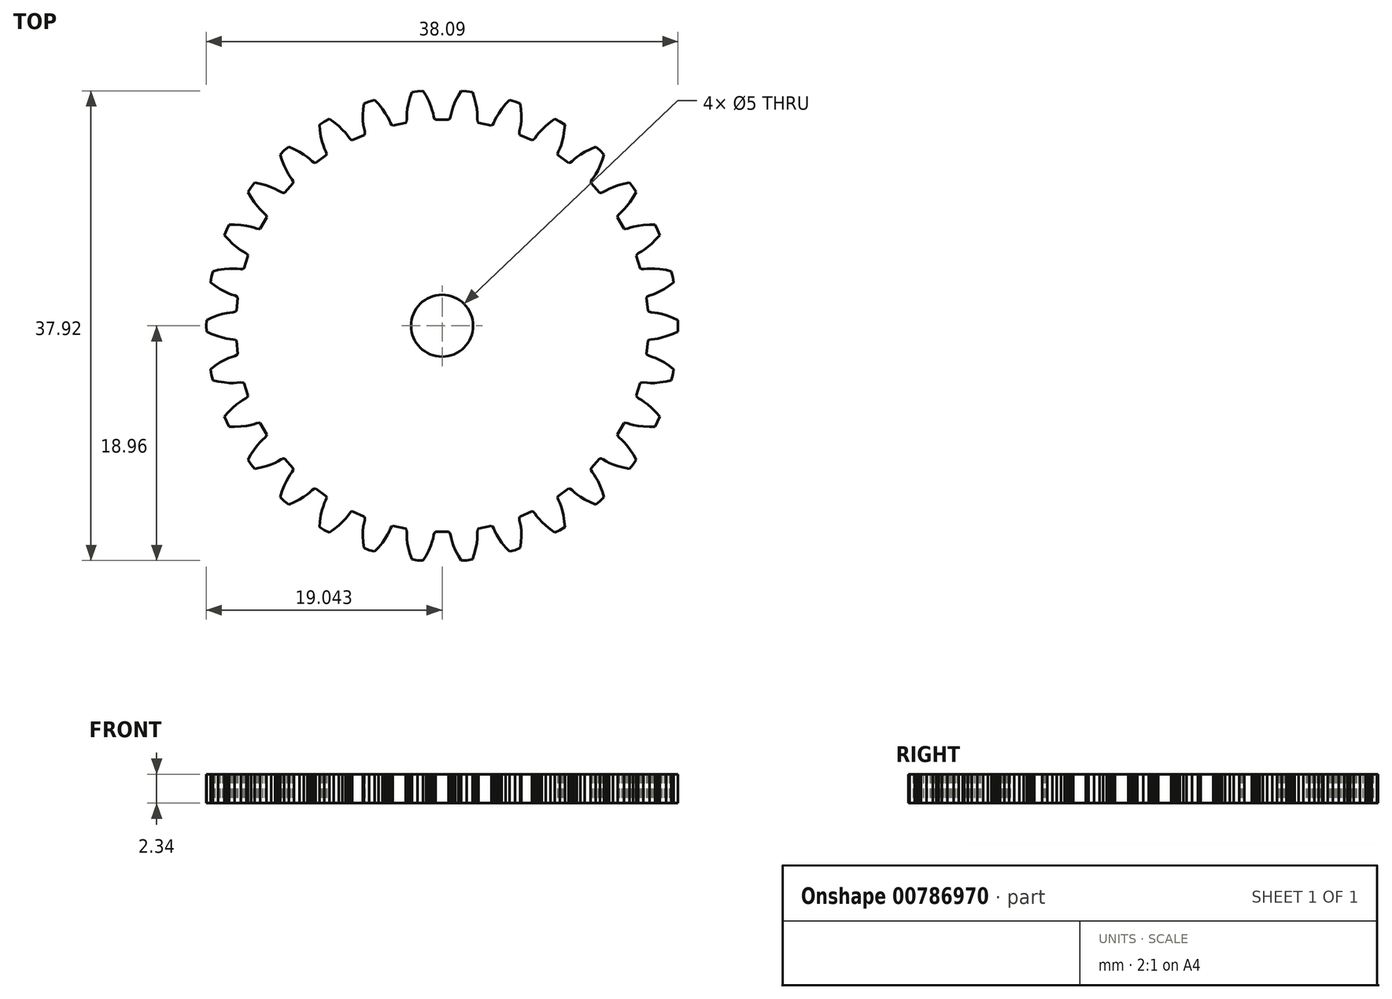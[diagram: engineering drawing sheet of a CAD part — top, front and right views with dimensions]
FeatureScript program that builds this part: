
annotation { "Feature Type Name" : "Feature", "Feature Type Description" : "" }
export const myFeature = defineFeature(function(context is Context, id is Id, definition is map)
    precondition{}
    {
        {
            var Q0;
            Q0=qCreatedBy(makeId("Top.planeOp"),FACE);
            var sketch = newSketch(context, id + "F0", { "sketchPlane" : qUnion([Q0])});
            skLineSegment(sketch, "E0", {"start": v(756.52, -239.33) * mm, "end": v(762.99, -215.17) * mm});
            skLineSegment(sketch, "E1", {"start": v(762.99, -215.17) * mm, "end": v(766.9, -190.46) * mm});
            skLineSegment(sketch, "E2", {"start": v(766.9, -190.46) * mm, "end": v(747.41, -175.84) * mm});
            skLineSegment(sketch, "E3", {"start": v(747.41, -175.84) * mm, "end": v(724.34, -160.92) * mm});
            skLineSegment(sketch, "E4", {"start": v(724.34, -160.92) * mm, "end": v(704.2, -149.81) * mm});
            skLineSegment(sketch, "E5", {"start": v(704.2, -149.81) * mm, "end": v(687.39, -142.02) * mm});
            skLineSegment(sketch, "E6", {"start": v(687.39, -142.02) * mm, "end": v(674.26, -137) * mm});
            skLineSegment(sketch, "E7", {"start": v(674.26, -137) * mm, "end": v(660.16, -132.73) * mm});
            skLineSegment(sketch, "E8", {"start": v(660.16, -132.73) * mm, "end": v(651.05, -128.15) * mm});
            skLineSegment(sketch, "E9", {"start": v(651.05, -128.15) * mm, "end": v(647, -123.28) * mm});
            skLineSegment(sketch, "E10", {"start": v(647, -123.28) * mm, "end": v(653.04, -65.76) * mm});
            skLineSegment(sketch, "E11", {"start": v(653.04, -65.76) * mm, "end": v(658.02, -61.84) * mm});
            skLineSegment(sketch, "E12", {"start": v(658.02, -61.84) * mm, "end": v(667.88, -59.26) * mm});
            skLineSegment(sketch, "E13", {"start": v(667.88, -59.26) * mm, "end": v(682.56, -58) * mm});
            skLineSegment(sketch, "E14", {"start": v(682.56, -58) * mm, "end": v(696.45, -55.83) * mm});
            skLineSegment(sketch, "E15", {"start": v(696.45, -55.83) * mm, "end": v(714.5, -51.7) * mm});
            skLineSegment(sketch, "E16", {"start": v(714.5, -51.7) * mm, "end": v(736.52, -45.02) * mm});
            skLineSegment(sketch, "E17", {"start": v(736.52, -45.02) * mm, "end": v(762.2, -35.23) * mm});
            skLineSegment(sketch, "E18", {"start": v(762.2, -35.23) * mm, "end": v(784.3, -24.98) * mm});
            skLineSegment(sketch, "E19", {"start": v(784.3, -24.98) * mm, "end": v(785.6, 0) * mm});
            skLineSegment(sketch, "E20", {"start": v(785.6, 0) * mm, "end": v(784.3, 24.98) * mm});
            skLineSegment(sketch, "E21", {"start": v(784.3, 24.98) * mm, "end": v(762.2, 35.23) * mm});
            skLineSegment(sketch, "E22", {"start": v(762.2, 35.23) * mm, "end": v(736.52, 45.02) * mm});
            skLineSegment(sketch, "E23", {"start": v(736.52, 45.02) * mm, "end": v(714.5, 51.7) * mm});
            skLineSegment(sketch, "E24", {"start": v(714.5, 51.7) * mm, "end": v(696.45, 55.83) * mm});
            skLineSegment(sketch, "E25", {"start": v(696.45, 55.83) * mm, "end": v(682.56, 58) * mm});
            skLineSegment(sketch, "E26", {"start": v(682.56, 58) * mm, "end": v(667.88, 59.26) * mm});
            skLineSegment(sketch, "E27", {"start": v(667.88, 59.26) * mm, "end": v(658.02, 61.84) * mm});
            skLineSegment(sketch, "E28", {"start": v(658.02, 61.84) * mm, "end": v(653.04, 65.76) * mm});
            skLineSegment(sketch, "E29", {"start": v(653.04, 65.76) * mm, "end": v(647, 123.28) * mm});
            skLineSegment(sketch, "E30", {"start": v(647, 123.28) * mm, "end": v(651.05, 128.15) * mm});
            skLineSegment(sketch, "E31", {"start": v(651.05, 128.15) * mm, "end": v(660.16, 132.73) * mm});
            skLineSegment(sketch, "E32", {"start": v(660.16, 132.73) * mm, "end": v(674.26, 137) * mm});
            skLineSegment(sketch, "E33", {"start": v(674.26, 137) * mm, "end": v(687.39, 142.02) * mm});
            skLineSegment(sketch, "E34", {"start": v(687.39, 142.02) * mm, "end": v(704.2, 149.81) * mm});
            skLineSegment(sketch, "E35", {"start": v(704.2, 149.81) * mm, "end": v(724.34, 160.92) * mm});
            skLineSegment(sketch, "E36", {"start": v(724.34, 160.92) * mm, "end": v(747.41, 175.84) * mm});
            skLineSegment(sketch, "E37", {"start": v(747.41, 175.84) * mm, "end": v(766.9, 190.46) * mm});
            skLineSegment(sketch, "E38", {"start": v(766.9, 190.46) * mm, "end": v(762.99, 215.17) * mm});
            skLineSegment(sketch, "E39", {"start": v(762.99, 215.17) * mm, "end": v(756.52, 239.33) * mm});
            skLineSegment(sketch, "E40", {"start": v(756.52, 239.33) * mm, "end": v(732.77, 244.76) * mm});
            skLineSegment(sketch, "E41", {"start": v(732.77, 244.76) * mm, "end": v(705.62, 249) * mm});
            skLineSegment(sketch, "E42", {"start": v(705.62, 249) * mm, "end": v(682.7, 250.96) * mm});
            skLineSegment(sketch, "E43", {"start": v(682.7, 250.96) * mm, "end": v(664.17, 251.24) * mm});
            skLineSegment(sketch, "E44", {"start": v(664.17, 251.24) * mm, "end": v(650.14, 250.48) * mm});
            skLineSegment(sketch, "E45", {"start": v(650.14, 250.48) * mm, "end": v(635.52, 248.65) * mm});
            skLineSegment(sketch, "E46", {"start": v(635.52, 248.65) * mm, "end": v(625.33, 249.13) * mm});
            skLineSegment(sketch, "E47", {"start": v(625.33, 249.13) * mm, "end": v(619.65, 251.93) * mm});
            skLineSegment(sketch, "E48", {"start": v(619.65, 251.93) * mm, "end": v(601.78, 306.93) * mm});
            skLineSegment(sketch, "E49", {"start": v(601.78, 306.93) * mm, "end": v(604.73, 312.54) * mm});
            skLineSegment(sketch, "E50", {"start": v(604.73, 312.54) * mm, "end": v(612.69, 318.91) * mm});
            skLineSegment(sketch, "E51", {"start": v(612.69, 318.91) * mm, "end": v(625.6, 326.03) * mm});
            skLineSegment(sketch, "E52", {"start": v(625.6, 326.03) * mm, "end": v(637.4, 333.66) * mm});
            skLineSegment(sketch, "E53", {"start": v(637.4, 333.66) * mm, "end": v(652.21, 344.78) * mm});
            skLineSegment(sketch, "E54", {"start": v(652.21, 344.78) * mm, "end": v(669.6, 359.83) * mm});
            skLineSegment(sketch, "E55", {"start": v(669.6, 359.83) * mm, "end": v(689.07, 379.22) * mm});
            skLineSegment(sketch, "E56", {"start": v(689.07, 379.22) * mm, "end": v(705.1, 397.58) * mm});
            skLineSegment(sketch, "E57", {"start": v(705.1, 397.58) * mm, "end": v(696.13, 420.93) * mm});
            skLineSegment(sketch, "E58", {"start": v(696.13, 420.93) * mm, "end": v(684.78, 443.21) * mm});
            skLineSegment(sketch, "E59", {"start": v(684.78, 443.21) * mm, "end": v(660.42, 443.59) * mm});
            skLineSegment(sketch, "E60", {"start": v(660.42, 443.59) * mm, "end": v(632.98, 442.1) * mm});
            skLineSegment(sketch, "E61", {"start": v(632.98, 442.1) * mm, "end": v(610.15, 439.24) * mm});
            skLineSegment(sketch, "E62", {"start": v(610.15, 439.24) * mm, "end": v(591.97, 435.67) * mm});
            skLineSegment(sketch, "E63", {"start": v(591.97, 435.67) * mm, "end": v(578.41, 432) * mm});
            skLineSegment(sketch, "E64", {"start": v(578.41, 432) * mm, "end": v(564.49, 427.18) * mm});
            skLineSegment(sketch, "E65", {"start": v(564.49, 427.18) * mm, "end": v(554.43, 425.53) * mm});
            skLineSegment(sketch, "E66", {"start": v(554.43, 425.53) * mm, "end": v(548.28, 427.08) * mm});
            skLineSegment(sketch, "E67", {"start": v(548.28, 427.08) * mm, "end": v(519.37, 477.17) * mm});
            skLineSegment(sketch, "E68", {"start": v(519.37, 477.17) * mm, "end": v(521.09, 483.27) * mm});
            skLineSegment(sketch, "E69", {"start": v(521.09, 483.27) * mm, "end": v(527.55, 491.16) * mm});
            skLineSegment(sketch, "E70", {"start": v(527.55, 491.16) * mm, "end": v(538.7, 500.8) * mm});
            skLineSegment(sketch, "E71", {"start": v(538.7, 500.8) * mm, "end": v(548.65, 510.72) * mm});
            skLineSegment(sketch, "E72", {"start": v(548.65, 510.72) * mm, "end": v(560.83, 524.67) * mm});
            skLineSegment(sketch, "E73", {"start": v(560.83, 524.67) * mm, "end": v(574.71, 543.02) * mm});
            skLineSegment(sketch, "E74", {"start": v(574.71, 543.02) * mm, "end": v(589.72, 566.03) * mm});
            skLineSegment(sketch, "E75", {"start": v(589.72, 566.03) * mm, "end": v(601.58, 587.32) * mm});
            skLineSegment(sketch, "E76", {"start": v(601.58, 587.32) * mm, "end": v(587.96, 608.3) * mm});
            skLineSegment(sketch, "E77", {"start": v(587.96, 608.3) * mm, "end": v(572.22, 627.73) * mm});
            skLineSegment(sketch, "E78", {"start": v(572.22, 627.73) * mm, "end": v(548.31, 623.03) * mm});
            skLineSegment(sketch, "E79", {"start": v(548.31, 623.03) * mm, "end": v(521.78, 615.87) * mm});
            skLineSegment(sketch, "E80", {"start": v(521.78, 615.87) * mm, "end": v(500.05, 608.33) * mm});
            skLineSegment(sketch, "E81", {"start": v(500.05, 608.33) * mm, "end": v(483.01, 601.06) * mm});
            skLineSegment(sketch, "E82", {"start": v(483.01, 601.06) * mm, "end": v(470.5, 594.65) * mm});
            skLineSegment(sketch, "E83", {"start": v(470.5, 594.65) * mm, "end": v(457.89, 587.04) * mm});
            skLineSegment(sketch, "E84", {"start": v(457.89, 587.04) * mm, "end": v(448.4, 583.33) * mm});
            skLineSegment(sketch, "E85", {"start": v(448.4, 583.33) * mm, "end": v(442.06, 583.58) * mm});
            skLineSegment(sketch, "E86", {"start": v(442.06, 583.58) * mm, "end": v(403.36, 626.56) * mm});
            skLineSegment(sketch, "E87", {"start": v(403.36, 626.56) * mm, "end": v(403.77, 632.88) * mm});
            skLineSegment(sketch, "E88", {"start": v(403.77, 632.88) * mm, "end": v(408.45, 641.94) * mm});
            skLineSegment(sketch, "E89", {"start": v(408.45, 641.94) * mm, "end": v(417.35, 653.69) * mm});
            skLineSegment(sketch, "E90", {"start": v(417.35, 653.69) * mm, "end": v(425.03, 665.46) * mm});
            skLineSegment(sketch, "E91", {"start": v(425.03, 665.46) * mm, "end": v(434.04, 681.64) * mm});
            skLineSegment(sketch, "E92", {"start": v(434.04, 681.64) * mm, "end": v(443.8, 702.47) * mm});
            skLineSegment(sketch, "E93", {"start": v(443.8, 702.47) * mm, "end": v(453.7, 728.1) * mm});
            skLineSegment(sketch, "E94", {"start": v(453.7, 728.1) * mm, "end": v(460.88, 751.39) * mm});
            skLineSegment(sketch, "E95", {"start": v(460.88, 751.39) * mm, "end": v(443.2, 769.07) * mm});
            skLineSegment(sketch, "E96", {"start": v(443.2, 769.07) * mm, "end": v(423.75, 784.81) * mm});
            skLineSegment(sketch, "E97", {"start": v(423.75, 784.81) * mm, "end": v(401.35, 775.25) * mm});
            skLineSegment(sketch, "E98", {"start": v(401.35, 775.25) * mm, "end": v(376.89, 762.72) * mm});
            skLineSegment(sketch, "E99", {"start": v(376.89, 762.72) * mm, "end": v(357.2, 750.83) * mm});
            skLineSegment(sketch, "E100", {"start": v(357.2, 750.83) * mm, "end": v(342.04, 740.18) * mm});
            skLineSegment(sketch, "E101", {"start": v(342.04, 740.18) * mm, "end": v(331.14, 731.31) * mm});
            skLineSegment(sketch, "E102", {"start": v(331.14, 731.31) * mm, "end": v(320.38, 721.24) * mm});
            skLineSegment(sketch, "E103", {"start": v(320.38, 721.24) * mm, "end": v(311.86, 715.64) * mm});
            skLineSegment(sketch, "E104", {"start": v(311.86, 715.64) * mm, "end": v(305.62, 714.56) * mm});
            skLineSegment(sketch, "E105", {"start": v(305.62, 714.56) * mm, "end": v(258.83, 748.56) * mm});
            skLineSegment(sketch, "E106", {"start": v(258.83, 748.56) * mm, "end": v(257.92, 754.83) * mm});
            skLineSegment(sketch, "E107", {"start": v(257.92, 754.83) * mm, "end": v(260.62, 764.66) * mm});
            skLineSegment(sketch, "E108", {"start": v(260.62, 764.66) * mm, "end": v(266.87, 778) * mm});
            skLineSegment(sketch, "E109", {"start": v(266.87, 778) * mm, "end": v(271.93, 791.11) * mm});
            skLineSegment(sketch, "E110", {"start": v(271.93, 791.11) * mm, "end": v(277.39, 808.82) * mm});
            skLineSegment(sketch, "E111", {"start": v(277.39, 808.82) * mm, "end": v(282.6, 831.22) * mm});
            skLineSegment(sketch, "E112", {"start": v(282.6, 831.22) * mm, "end": v(286.96, 858.35) * mm});
            skLineSegment(sketch, "E113", {"start": v(286.96, 858.35) * mm, "end": v(289.14, 882.62) * mm});
            skLineSegment(sketch, "E114", {"start": v(289.14, 882.62) * mm, "end": v(268.16, 896.24) * mm});
            skLineSegment(sketch, "E115", {"start": v(268.16, 896.24) * mm, "end": v(245.87, 907.6) * mm});
            skLineSegment(sketch, "E116", {"start": v(245.87, 907.6) * mm, "end": v(225.94, 893.58) * mm});
            skLineSegment(sketch, "E117", {"start": v(225.94, 893.58) * mm, "end": v(204.63, 876.24) * mm});
            skLineSegment(sketch, "E118", {"start": v(204.63, 876.24) * mm, "end": v(187.83, 860.52) * mm});
            skLineSegment(sketch, "E119", {"start": v(187.83, 860.52) * mm, "end": v(175.23, 846.94) * mm});
            skLineSegment(sketch, "E120", {"start": v(175.23, 846.94) * mm, "end": v(166.4, 836) * mm});
            skLineSegment(sketch, "E121", {"start": v(166.4, 836) * mm, "end": v(157.98, 823.92) * mm});
            skLineSegment(sketch, "E122", {"start": v(157.98, 823.92) * mm, "end": v(150.81, 816.67) * mm});
            skLineSegment(sketch, "E123", {"start": v(150.81, 816.67) * mm, "end": v(144.93, 814.32) * mm});
            skLineSegment(sketch, "E124", {"start": v(144.93, 814.32) * mm, "end": v(92.1, 837.84) * mm});
            skLineSegment(sketch, "E125", {"start": v(92.1, 837.84) * mm, "end": v(89.9, 843.79) * mm});
            skLineSegment(sketch, "E126", {"start": v(89.9, 843.79) * mm, "end": v(90.5, 853.97) * mm});
            skLineSegment(sketch, "E127", {"start": v(90.5, 853.97) * mm, "end": v(93.84, 868.32) * mm});
            skLineSegment(sketch, "E128", {"start": v(93.84, 868.32) * mm, "end": v(96.06, 882.2) * mm});
            skLineSegment(sketch, "E129", {"start": v(96.06, 882.2) * mm, "end": v(97.72, 900.64) * mm});
            skLineSegment(sketch, "E130", {"start": v(97.72, 900.64) * mm, "end": v(98.16, 923.64) * mm});
            skLineSegment(sketch, "E131", {"start": v(98.16, 923.64) * mm, "end": v(96.78, 951.09) * mm});
            skLineSegment(sketch, "E132", {"start": v(96.78, 951.09) * mm, "end": v(93.86, 975.27) * mm});
            skLineSegment(sketch, "E133", {"start": v(93.86, 975.27) * mm, "end": v(70.51, 984.24) * mm});
            skLineSegment(sketch, "E134", {"start": v(70.51, 984.24) * mm, "end": v(46.35, 990.71) * mm});
            skLineSegment(sketch, "E135", {"start": v(46.35, 990.71) * mm, "end": v(29.77, 972.86) * mm});
            skLineSegment(sketch, "E136", {"start": v(29.77, 972.86) * mm, "end": v(12.53, 951.47) * mm});
            skLineSegment(sketch, "E137", {"start": v(12.53, 951.47) * mm, "end": v(-0.63, 932.6) * mm});
            skLineSegment(sketch, "E138", {"start": v(-0.63, 932.6) * mm, "end": v(-10.14, 916.7) * mm});
            skLineSegment(sketch, "E139", {"start": v(-10.14, 916.7) * mm, "end": v(-16.5, 904.17) * mm});
            skLineSegment(sketch, "E140", {"start": v(-16.5, 904.17) * mm, "end": v(-22.22, 890.59) * mm});
            skLineSegment(sketch, "E141", {"start": v(-22.22, 890.59) * mm, "end": v(-27.73, 882) * mm});
            skLineSegment(sketch, "E142", {"start": v(-27.73, 882) * mm, "end": v(-33, 878.49) * mm});
            skLineSegment(sketch, "E143", {"start": v(-33, 878.49) * mm, "end": v(-89.57, 890.51) * mm});
            skLineSegment(sketch, "E144", {"start": v(-89.57, 890.51) * mm, "end": v(-92.95, 895.87) * mm});
            skLineSegment(sketch, "E145", {"start": v(-92.95, 895.87) * mm, "end": v(-94.48, 905.95) * mm});
            skLineSegment(sketch, "E146", {"start": v(-94.48, 905.95) * mm, "end": v(-94.2, 920.68) * mm});
            skLineSegment(sketch, "E147", {"start": v(-94.2, 920.68) * mm, "end": v(-94.9, 934.72) * mm});
            skLineSegment(sketch, "E148", {"start": v(-94.9, 934.72) * mm, "end": v(-97.12, 953.1) * mm});
            skLineSegment(sketch, "E149", {"start": v(-97.12, 953.1) * mm, "end": v(-101.46, 975.7) * mm});
            skLineSegment(sketch, "E150", {"start": v(-101.46, 975.7) * mm, "end": v(-108.52, 1002.25) * mm});
            skLineSegment(sketch, "E151", {"start": v(-108.52, 1002.25) * mm, "end": v(-116.4, 1025.3) * mm});
            skLineSegment(sketch, "E152", {"start": v(-116.4, 1025.3) * mm, "end": v(-141.11, 1029.22) * mm});
            skLineSegment(sketch, "E153", {"start": v(-141.11, 1029.22) * mm, "end": v(-166.09, 1030.53) * mm});
            skLineSegment(sketch, "E154", {"start": v(-166.09, 1030.53) * mm, "end": v(-178.6, 1009.62) * mm});
            skLineSegment(sketch, "E155", {"start": v(-178.6, 1009.62) * mm, "end": v(-191.02, 985.11) * mm});
            skLineSegment(sketch, "E156", {"start": v(-191.02, 985.11) * mm, "end": v(-199.96, 963.92) * mm});
            skLineSegment(sketch, "E157", {"start": v(-199.96, 963.92) * mm, "end": v(-205.96, 946.39) * mm});
            skLineSegment(sketch, "E158", {"start": v(-205.96, 946.39) * mm, "end": v(-209.57, 932.8) * mm});
            skLineSegment(sketch, "E159", {"start": v(-209.57, 932.8) * mm, "end": v(-212.35, 918.34) * mm});
            skLineSegment(sketch, "E160", {"start": v(-212.35, 918.34) * mm, "end": v(-215.95, 908.8) * mm});
            skLineSegment(sketch, "E161", {"start": v(-215.95, 908.8) * mm, "end": v(-220.37, 904.26) * mm});
            skLineSegment(sketch, "E162", {"start": v(-220.37, 904.26) * mm, "end": v(-278.2, 904.26) * mm});
            skLineSegment(sketch, "E163", {"start": v(-278.2, 904.26) * mm, "end": v(-282.62, 908.8) * mm});
            skLineSegment(sketch, "E164", {"start": v(-282.62, 908.8) * mm, "end": v(-286.22, 918.34) * mm});
            skLineSegment(sketch, "E165", {"start": v(-286.22, 918.34) * mm, "end": v(-289, 932.8) * mm});
            skLineSegment(sketch, "E166", {"start": v(-289, 932.8) * mm, "end": v(-292.61, 946.39) * mm});
            skLineSegment(sketch, "E167", {"start": v(-292.61, 946.39) * mm, "end": v(-298.6, 963.92) * mm});
            skLineSegment(sketch, "E168", {"start": v(-298.6, 963.92) * mm, "end": v(-307.55, 985.11) * mm});
            skLineSegment(sketch, "E169", {"start": v(-307.55, 985.11) * mm, "end": v(-319.98, 1009.62) * mm});
            skLineSegment(sketch, "E170", {"start": v(-319.98, 1009.62) * mm, "end": v(-332.48, 1030.53) * mm});
            skLineSegment(sketch, "E171", {"start": v(-332.48, 1030.53) * mm, "end": v(-357.46, 1029.22) * mm});
            skLineSegment(sketch, "E172", {"start": v(-357.46, 1029.22) * mm, "end": v(-382.16, 1025.3) * mm});
            skLineSegment(sketch, "E173", {"start": v(-382.16, 1025.3) * mm, "end": v(-390.05, 1002.25) * mm});
            skLineSegment(sketch, "E174", {"start": v(-390.05, 1002.25) * mm, "end": v(-397.1, 975.7) * mm});
            skLineSegment(sketch, "E175", {"start": v(-397.1, 975.7) * mm, "end": v(-401.45, 953.1) * mm});
            skLineSegment(sketch, "E176", {"start": v(-401.45, 953.1) * mm, "end": v(-403.67, 934.72) * mm});
            skLineSegment(sketch, "E177", {"start": v(-403.67, 934.72) * mm, "end": v(-404.38, 920.68) * mm});
            skLineSegment(sketch, "E178", {"start": v(-404.38, 920.68) * mm, "end": v(-404.09, 905.95) * mm});
            skLineSegment(sketch, "E179", {"start": v(-404.09, 905.95) * mm, "end": v(-405.62, 895.87) * mm});
            skLineSegment(sketch, "E180", {"start": v(-405.62, 895.87) * mm, "end": v(-409, 890.51) * mm});
            skLineSegment(sketch, "E181", {"start": v(-409, 890.51) * mm, "end": v(-465.58, 878.49) * mm});
            skLineSegment(sketch, "E182", {"start": v(-465.58, 878.49) * mm, "end": v(-470.85, 882) * mm});
            skLineSegment(sketch, "E183", {"start": v(-470.85, 882) * mm, "end": v(-476.35, 890.59) * mm});
            skLineSegment(sketch, "E184", {"start": v(-476.35, 890.59) * mm, "end": v(-482.08, 904.17) * mm});
            skLineSegment(sketch, "E185", {"start": v(-482.08, 904.17) * mm, "end": v(-488.43, 916.7) * mm});
            skLineSegment(sketch, "E186", {"start": v(-488.43, 916.7) * mm, "end": v(-497.94, 932.6) * mm});
            skLineSegment(sketch, "E187", {"start": v(-497.94, 932.6) * mm, "end": v(-511.1, 951.47) * mm});
            skLineSegment(sketch, "E188", {"start": v(-511.1, 951.47) * mm, "end": v(-528.35, 972.86) * mm});
            skLineSegment(sketch, "E189", {"start": v(-528.35, 972.86) * mm, "end": v(-544.92, 990.71) * mm});
            skLineSegment(sketch, "E190", {"start": v(-544.92, 990.71) * mm, "end": v(-569.08, 984.24) * mm});
            skLineSegment(sketch, "E191", {"start": v(-569.08, 984.24) * mm, "end": v(-592.43, 975.27) * mm});
            skLineSegment(sketch, "E192", {"start": v(-592.43, 975.27) * mm, "end": v(-595.35, 951.09) * mm});
            skLineSegment(sketch, "E193", {"start": v(-595.35, 951.09) * mm, "end": v(-596.74, 923.64) * mm});
            skLineSegment(sketch, "E194", {"start": v(-596.74, 923.64) * mm, "end": v(-596.29, 900.64) * mm});
            skLineSegment(sketch, "E195", {"start": v(-596.29, 900.64) * mm, "end": v(-594.63, 882.2) * mm});
            skLineSegment(sketch, "E196", {"start": v(-594.63, 882.2) * mm, "end": v(-592.4, 868.32) * mm});
            skLineSegment(sketch, "E197", {"start": v(-592.4, 868.32) * mm, "end": v(-589.06, 853.97) * mm});
            skLineSegment(sketch, "E198", {"start": v(-589.06, 853.97) * mm, "end": v(-588.47, 843.79) * mm});
            skLineSegment(sketch, "E199", {"start": v(-588.47, 843.79) * mm, "end": v(-590.66, 837.84) * mm});
            skLineSegment(sketch, "E200", {"start": v(-590.66, 837.84) * mm, "end": v(-643.5, 814.32) * mm});
            skLineSegment(sketch, "E201", {"start": v(-643.5, 814.32) * mm, "end": v(-649.38, 816.67) * mm});
            skLineSegment(sketch, "E202", {"start": v(-649.38, 816.67) * mm, "end": v(-656.55, 823.92) * mm});
            skLineSegment(sketch, "E203", {"start": v(-656.55, 823.92) * mm, "end": v(-664.98, 836) * mm});
            skLineSegment(sketch, "E204", {"start": v(-664.98, 836) * mm, "end": v(-673.8, 846.94) * mm});
            skLineSegment(sketch, "E205", {"start": v(-673.8, 846.94) * mm, "end": v(-686.4, 860.52) * mm});
            skLineSegment(sketch, "E206", {"start": v(-686.4, 860.52) * mm, "end": v(-703.2, 876.24) * mm});
            skLineSegment(sketch, "E207", {"start": v(-703.2, 876.24) * mm, "end": v(-724.52, 893.58) * mm});
            skLineSegment(sketch, "E208", {"start": v(-724.52, 893.58) * mm, "end": v(-744.44, 907.6) * mm});
            skLineSegment(sketch, "E209", {"start": v(-744.44, 907.6) * mm, "end": v(-766.73, 896.24) * mm});
            skLineSegment(sketch, "E210", {"start": v(-766.73, 896.24) * mm, "end": v(-787.7, 882.62) * mm});
            skLineSegment(sketch, "E211", {"start": v(-787.7, 882.62) * mm, "end": v(-785.53, 858.35) * mm});
            skLineSegment(sketch, "E212", {"start": v(-785.53, 858.35) * mm, "end": v(-781.18, 831.22) * mm});
            skLineSegment(sketch, "E213", {"start": v(-781.18, 831.22) * mm, "end": v(-775.96, 808.82) * mm});
            skLineSegment(sketch, "E214", {"start": v(-775.96, 808.82) * mm, "end": v(-770.5, 791.11) * mm});
            skLineSegment(sketch, "E215", {"start": v(-770.5, 791.11) * mm, "end": v(-765.44, 778) * mm});
            skLineSegment(sketch, "E216", {"start": v(-765.44, 778) * mm, "end": v(-759.19, 764.66) * mm});
            skLineSegment(sketch, "E217", {"start": v(-759.19, 764.66) * mm, "end": v(-756.5, 754.83) * mm});
            skLineSegment(sketch, "E218", {"start": v(-756.5, 754.83) * mm, "end": v(-757.4, 748.56) * mm});
            skLineSegment(sketch, "E219", {"start": v(-757.4, 748.56) * mm, "end": v(-804.2, 714.56) * mm});
            skLineSegment(sketch, "E220", {"start": v(-804.2, 714.56) * mm, "end": v(-810.44, 715.64) * mm});
            skLineSegment(sketch, "E221", {"start": v(-810.44, 715.64) * mm, "end": v(-818.95, 721.24) * mm});
            skLineSegment(sketch, "E222", {"start": v(-818.95, 721.24) * mm, "end": v(-829.71, 731.31) * mm});
            skLineSegment(sketch, "E223", {"start": v(-829.71, 731.31) * mm, "end": v(-840.61, 740.18) * mm});
            skLineSegment(sketch, "E224", {"start": v(-840.61, 740.18) * mm, "end": v(-855.77, 750.83) * mm});
            skLineSegment(sketch, "E225", {"start": v(-855.77, 750.83) * mm, "end": v(-875.46, 762.72) * mm});
            skLineSegment(sketch, "E226", {"start": v(-875.46, 762.72) * mm, "end": v(-899.92, 775.25) * mm});
            skLineSegment(sketch, "E227", {"start": v(-899.92, 775.25) * mm, "end": v(-922.32, 784.81) * mm});
            skLineSegment(sketch, "E228", {"start": v(-922.32, 784.81) * mm, "end": v(-941.76, 769.07) * mm});
            skLineSegment(sketch, "E229", {"start": v(-941.76, 769.07) * mm, "end": v(-959.45, 751.39) * mm});
            skLineSegment(sketch, "E230", {"start": v(-959.45, 751.39) * mm, "end": v(-952.28, 728.1) * mm});
            skLineSegment(sketch, "E231", {"start": v(-952.28, 728.1) * mm, "end": v(-942.38, 702.47) * mm});
            skLineSegment(sketch, "E232", {"start": v(-942.38, 702.47) * mm, "end": v(-932.61, 681.64) * mm});
            skLineSegment(sketch, "E233", {"start": v(-932.61, 681.64) * mm, "end": v(-923.6, 665.46) * mm});
            skLineSegment(sketch, "E234", {"start": v(-923.6, 665.46) * mm, "end": v(-915.92, 653.69) * mm});
            skLineSegment(sketch, "E235", {"start": v(-915.92, 653.69) * mm, "end": v(-907.03, 641.94) * mm});
            skLineSegment(sketch, "E236", {"start": v(-907.03, 641.94) * mm, "end": v(-902.35, 632.88) * mm});
            skLineSegment(sketch, "E237", {"start": v(-902.35, 632.88) * mm, "end": v(-901.93, 626.56) * mm});
            skLineSegment(sketch, "E238", {"start": v(-901.93, 626.56) * mm, "end": v(-940.63, 583.58) * mm});
            skLineSegment(sketch, "E239", {"start": v(-940.63, 583.58) * mm, "end": v(-946.96, 583.33) * mm});
            skLineSegment(sketch, "E240", {"start": v(-946.96, 583.33) * mm, "end": v(-956.46, 587.04) * mm});
            skLineSegment(sketch, "E241", {"start": v(-956.46, 587.04) * mm, "end": v(-969.07, 594.65) * mm});
            skLineSegment(sketch, "E242", {"start": v(-969.07, 594.65) * mm, "end": v(-981.58, 601.06) * mm});
            skLineSegment(sketch, "E243", {"start": v(-981.58, 601.06) * mm, "end": v(-998.62, 608.33) * mm});
            skLineSegment(sketch, "E244", {"start": v(-998.62, 608.33) * mm, "end": v(-1020.35, 615.87) * mm});
            skLineSegment(sketch, "E245", {"start": v(-1020.35, 615.87) * mm, "end": v(-1046.88, 623.03) * mm});
            skLineSegment(sketch, "E246", {"start": v(-1046.88, 623.03) * mm, "end": v(-1070.79, 627.73) * mm});
            skLineSegment(sketch, "E247", {"start": v(-1070.79, 627.73) * mm, "end": v(-1086.53, 608.3) * mm});
            skLineSegment(sketch, "E248", {"start": v(-1086.53, 608.3) * mm, "end": v(-1100.15, 587.32) * mm});
            skLineSegment(sketch, "E249", {"start": v(-1100.15, 587.32) * mm, "end": v(-1088.3, 566.03) * mm});
            skLineSegment(sketch, "E250", {"start": v(-1088.3, 566.03) * mm, "end": v(-1073.28, 543.02) * mm});
            skLineSegment(sketch, "E251", {"start": v(-1073.28, 543.02) * mm, "end": v(-1059.4, 524.67) * mm});
            skLineSegment(sketch, "E252", {"start": v(-1059.4, 524.67) * mm, "end": v(-1047.22, 510.72) * mm});
            skLineSegment(sketch, "E253", {"start": v(-1047.22, 510.72) * mm, "end": v(-1037.26, 500.8) * mm});
            skLineSegment(sketch, "E254", {"start": v(-1037.26, 500.8) * mm, "end": v(-1026.12, 491.16) * mm});
            skLineSegment(sketch, "E255", {"start": v(-1026.12, 491.16) * mm, "end": v(-1019.66, 483.27) * mm});
            skLineSegment(sketch, "E256", {"start": v(-1019.66, 483.27) * mm, "end": v(-1017.94, 477.17) * mm});
            skLineSegment(sketch, "E257", {"start": v(-1017.94, 477.17) * mm, "end": v(-1046.86, 427.08) * mm});
            skLineSegment(sketch, "E258", {"start": v(-1046.86, 427.08) * mm, "end": v(-1053, 425.53) * mm});
            skLineSegment(sketch, "E259", {"start": v(-1053, 425.53) * mm, "end": v(-1063.06, 427.18) * mm});
            skLineSegment(sketch, "E260", {"start": v(-1063.06, 427.18) * mm, "end": v(-1076.98, 432) * mm});
            skLineSegment(sketch, "E261", {"start": v(-1076.98, 432) * mm, "end": v(-1090.55, 435.67) * mm});
            skLineSegment(sketch, "E262", {"start": v(-1090.55, 435.67) * mm, "end": v(-1108.72, 439.24) * mm});
            skLineSegment(sketch, "E263", {"start": v(-1108.72, 439.24) * mm, "end": v(-1131.55, 442.1) * mm});
            skLineSegment(sketch, "E264", {"start": v(-1131.55, 442.1) * mm, "end": v(-1158.99, 443.59) * mm});
            skLineSegment(sketch, "E265", {"start": v(-1158.99, 443.59) * mm, "end": v(-1183.35, 443.21) * mm});
            skLineSegment(sketch, "E266", {"start": v(-1183.35, 443.21) * mm, "end": v(-1194.7, 420.93) * mm});
            skLineSegment(sketch, "E267", {"start": v(-1194.7, 420.93) * mm, "end": v(-1203.67, 397.58) * mm});
            skLineSegment(sketch, "E268", {"start": v(-1203.67, 397.58) * mm, "end": v(-1187.65, 379.22) * mm});
            skLineSegment(sketch, "E269", {"start": v(-1187.65, 379.22) * mm, "end": v(-1168.18, 359.83) * mm});
            skLineSegment(sketch, "E270", {"start": v(-1168.18, 359.83) * mm, "end": v(-1150.78, 344.78) * mm});
            skLineSegment(sketch, "E271", {"start": v(-1150.78, 344.78) * mm, "end": v(-1135.96, 333.66) * mm});
            skLineSegment(sketch, "E272", {"start": v(-1135.96, 333.66) * mm, "end": v(-1124.16, 326.03) * mm});
            skLineSegment(sketch, "E273", {"start": v(-1124.16, 326.03) * mm, "end": v(-1111.26, 318.91) * mm});
            skLineSegment(sketch, "E274", {"start": v(-1111.26, 318.91) * mm, "end": v(-1103.3, 312.54) * mm});
            skLineSegment(sketch, "E275", {"start": v(-1103.3, 312.54) * mm, "end": v(-1100.35, 306.93) * mm});
            skLineSegment(sketch, "E276", {"start": v(-1100.35, 306.93) * mm, "end": v(-1118.22, 251.93) * mm});
            skLineSegment(sketch, "E277", {"start": v(-1118.22, 251.93) * mm, "end": v(-1123.9, 249.13) * mm});
            skLineSegment(sketch, "E278", {"start": v(-1123.9, 249.13) * mm, "end": v(-1134.09, 248.65) * mm});
            skLineSegment(sketch, "E279", {"start": v(-1134.09, 248.65) * mm, "end": v(-1148.71, 250.48) * mm});
            skLineSegment(sketch, "E280", {"start": v(-1148.71, 250.48) * mm, "end": v(-1162.74, 251.24) * mm});
            skLineSegment(sketch, "E281", {"start": v(-1162.74, 251.24) * mm, "end": v(-1181.27, 250.96) * mm});
            skLineSegment(sketch, "E282", {"start": v(-1181.27, 250.96) * mm, "end": v(-1204.19, 249) * mm});
            skLineSegment(sketch, "E283", {"start": v(-1204.19, 249) * mm, "end": v(-1231.34, 244.76) * mm});
            skLineSegment(sketch, "E284", {"start": v(-1231.34, 244.76) * mm, "end": v(-1255.09, 239.33) * mm});
            skLineSegment(sketch, "E285", {"start": v(-1255.09, 239.33) * mm, "end": v(-1261.56, 215.17) * mm});
            skLineSegment(sketch, "E286", {"start": v(-1261.56, 215.17) * mm, "end": v(-1265.47, 190.46) * mm});
            skLineSegment(sketch, "E287", {"start": v(-1265.47, 190.46) * mm, "end": v(-1245.99, 175.84) * mm});
            skLineSegment(sketch, "E288", {"start": v(-1245.99, 175.84) * mm, "end": v(-1222.9, 160.92) * mm});
            skLineSegment(sketch, "E289", {"start": v(-1222.9, 160.92) * mm, "end": v(-1202.77, 149.81) * mm});
            skLineSegment(sketch, "E290", {"start": v(-1202.77, 149.81) * mm, "end": v(-1185.96, 142.02) * mm});
            skLineSegment(sketch, "E291", {"start": v(-1185.96, 142.02) * mm, "end": v(-1172.83, 137) * mm});
            skLineSegment(sketch, "E292", {"start": v(-1172.83, 137) * mm, "end": v(-1158.73, 132.73) * mm});
            skLineSegment(sketch, "E293", {"start": v(-1158.73, 132.73) * mm, "end": v(-1149.62, 128.15) * mm});
            skLineSegment(sketch, "E294", {"start": v(-1149.62, 128.15) * mm, "end": v(-1145.57, 123.28) * mm});
            skLineSegment(sketch, "E295", {"start": v(-1145.57, 123.28) * mm, "end": v(-1151.61, 65.76) * mm});
            skLineSegment(sketch, "E296", {"start": v(-1151.61, 65.76) * mm, "end": v(-1156.59, 61.84) * mm});
            skLineSegment(sketch, "E297", {"start": v(-1156.59, 61.84) * mm, "end": v(-1166.45, 59.26) * mm});
            skLineSegment(sketch, "E298", {"start": v(-1166.45, 59.26) * mm, "end": v(-1181.14, 58) * mm});
            skLineSegment(sketch, "E299", {"start": v(-1181.14, 58) * mm, "end": v(-1195.02, 55.83) * mm});
            skLineSegment(sketch, "E300", {"start": v(-1195.02, 55.83) * mm, "end": v(-1213.08, 51.7) * mm});
            skLineSegment(sketch, "E301", {"start": v(-1213.08, 51.7) * mm, "end": v(-1235.09, 45.02) * mm});
            skLineSegment(sketch, "E302", {"start": v(-1235.09, 45.02) * mm, "end": v(-1260.76, 35.23) * mm});
            skLineSegment(sketch, "E303", {"start": v(-1260.76, 35.23) * mm, "end": v(-1282.87, 24.98) * mm});
            skLineSegment(sketch, "E304", {"start": v(-1282.87, 24.98) * mm, "end": v(-1284.17, 0) * mm});
            skLineSegment(sketch, "E305", {"start": v(-1284.17, 0) * mm, "end": v(-1282.87, -24.98) * mm});
            skLineSegment(sketch, "E306", {"start": v(-1282.87, -24.98) * mm, "end": v(-1260.76, -35.23) * mm});
            skLineSegment(sketch, "E307", {"start": v(-1260.76, -35.23) * mm, "end": v(-1235.09, -45.02) * mm});
            skLineSegment(sketch, "E308", {"start": v(-1235.09, -45.02) * mm, "end": v(-1213.08, -51.7) * mm});
            skLineSegment(sketch, "E309", {"start": v(-1213.08, -51.7) * mm, "end": v(-1195.02, -55.83) * mm});
            skLineSegment(sketch, "E310", {"start": v(-1195.02, -55.83) * mm, "end": v(-1181.14, -58) * mm});
            skLineSegment(sketch, "E311", {"start": v(-1181.14, -58) * mm, "end": v(-1166.45, -59.26) * mm});
            skLineSegment(sketch, "E312", {"start": v(-1166.45, -59.26) * mm, "end": v(-1156.59, -61.84) * mm});
            skLineSegment(sketch, "E313", {"start": v(-1156.59, -61.84) * mm, "end": v(-1151.61, -65.76) * mm});
            skLineSegment(sketch, "E314", {"start": v(-1151.61, -65.76) * mm, "end": v(-1145.57, -123.28) * mm});
            skLineSegment(sketch, "E315", {"start": v(-1145.57, -123.28) * mm, "end": v(-1149.62, -128.15) * mm});
            skLineSegment(sketch, "E316", {"start": v(-1149.62, -128.15) * mm, "end": v(-1158.73, -132.73) * mm});
            skLineSegment(sketch, "E317", {"start": v(-1158.73, -132.73) * mm, "end": v(-1172.83, -137) * mm});
            skLineSegment(sketch, "E318", {"start": v(-1172.83, -137) * mm, "end": v(-1185.96, -142.02) * mm});
            skLineSegment(sketch, "E319", {"start": v(-1185.96, -142.02) * mm, "end": v(-1202.77, -149.81) * mm});
            skLineSegment(sketch, "E320", {"start": v(-1202.77, -149.81) * mm, "end": v(-1222.9, -160.92) * mm});
            skLineSegment(sketch, "E321", {"start": v(-1222.9, -160.92) * mm, "end": v(-1245.99, -175.84) * mm});
            skLineSegment(sketch, "E322", {"start": v(-1245.99, -175.84) * mm, "end": v(-1265.47, -190.46) * mm});
            skLineSegment(sketch, "E323", {"start": v(-1265.47, -190.46) * mm, "end": v(-1261.56, -215.17) * mm});
            skLineSegment(sketch, "E324", {"start": v(-1261.56, -215.17) * mm, "end": v(-1255.09, -239.33) * mm});
            skLineSegment(sketch, "E325", {"start": v(-1255.09, -239.33) * mm, "end": v(-1231.34, -244.76) * mm});
            skLineSegment(sketch, "E326", {"start": v(-1231.34, -244.76) * mm, "end": v(-1204.19, -249) * mm});
            skLineSegment(sketch, "E327", {"start": v(-1204.19, -249) * mm, "end": v(-1181.27, -250.96) * mm});
            skLineSegment(sketch, "E328", {"start": v(-1181.27, -250.96) * mm, "end": v(-1162.74, -251.24) * mm});
            skLineSegment(sketch, "E329", {"start": v(-1162.74, -251.24) * mm, "end": v(-1148.71, -250.48) * mm});
            skLineSegment(sketch, "E330", {"start": v(-1148.71, -250.48) * mm, "end": v(-1134.09, -248.65) * mm});
            skLineSegment(sketch, "E331", {"start": v(-1134.09, -248.65) * mm, "end": v(-1123.9, -249.13) * mm});
            skLineSegment(sketch, "E332", {"start": v(-1123.9, -249.13) * mm, "end": v(-1118.22, -251.93) * mm});
            skLineSegment(sketch, "E333", {"start": v(-1118.22, -251.93) * mm, "end": v(-1100.35, -306.93) * mm});
            skLineSegment(sketch, "E334", {"start": v(-1100.35, -306.93) * mm, "end": v(-1103.3, -312.54) * mm});
            skLineSegment(sketch, "E335", {"start": v(-1103.3, -312.54) * mm, "end": v(-1111.26, -318.91) * mm});
            skLineSegment(sketch, "E336", {"start": v(-1111.26, -318.91) * mm, "end": v(-1124.16, -326.03) * mm});
            skLineSegment(sketch, "E337", {"start": v(-1124.16, -326.03) * mm, "end": v(-1135.96, -333.66) * mm});
            skLineSegment(sketch, "E338", {"start": v(-1135.96, -333.66) * mm, "end": v(-1150.78, -344.78) * mm});
            skLineSegment(sketch, "E339", {"start": v(-1150.78, -344.78) * mm, "end": v(-1168.18, -359.83) * mm});
            skLineSegment(sketch, "E340", {"start": v(-1168.18, -359.83) * mm, "end": v(-1187.65, -379.22) * mm});
            skLineSegment(sketch, "E341", {"start": v(-1187.65, -379.22) * mm, "end": v(-1203.67, -397.58) * mm});
            skLineSegment(sketch, "E342", {"start": v(-1203.67, -397.58) * mm, "end": v(-1194.7, -420.93) * mm});
            skLineSegment(sketch, "E343", {"start": v(-1194.7, -420.93) * mm, "end": v(-1183.35, -443.21) * mm});
            skLineSegment(sketch, "E344", {"start": v(-1183.35, -443.21) * mm, "end": v(-1158.99, -443.59) * mm});
            skLineSegment(sketch, "E345", {"start": v(-1158.99, -443.59) * mm, "end": v(-1131.55, -442.1) * mm});
            skLineSegment(sketch, "E346", {"start": v(-1131.55, -442.1) * mm, "end": v(-1108.72, -439.24) * mm});
            skLineSegment(sketch, "E347", {"start": v(-1108.72, -439.24) * mm, "end": v(-1090.55, -435.67) * mm});
            skLineSegment(sketch, "E348", {"start": v(-1090.55, -435.67) * mm, "end": v(-1076.98, -432) * mm});
            skLineSegment(sketch, "E349", {"start": v(-1076.98, -432) * mm, "end": v(-1063.06, -427.18) * mm});
            skLineSegment(sketch, "E350", {"start": v(-1063.06, -427.18) * mm, "end": v(-1053, -425.53) * mm});
            skLineSegment(sketch, "E351", {"start": v(-1053, -425.53) * mm, "end": v(-1046.86, -427.08) * mm});
            skLineSegment(sketch, "E352", {"start": v(-1046.86, -427.08) * mm, "end": v(-1017.94, -477.17) * mm});
            skLineSegment(sketch, "E353", {"start": v(-1017.94, -477.17) * mm, "end": v(-1019.66, -483.27) * mm});
            skLineSegment(sketch, "E354", {"start": v(-1019.66, -483.27) * mm, "end": v(-1026.12, -491.16) * mm});
            skLineSegment(sketch, "E355", {"start": v(-1026.12, -491.16) * mm, "end": v(-1037.26, -500.8) * mm});
            skLineSegment(sketch, "E356", {"start": v(-1037.26, -500.8) * mm, "end": v(-1047.22, -510.72) * mm});
            skLineSegment(sketch, "E357", {"start": v(-1047.22, -510.72) * mm, "end": v(-1059.4, -524.67) * mm});
            skLineSegment(sketch, "E358", {"start": v(-1059.4, -524.67) * mm, "end": v(-1073.28, -543.02) * mm});
            skLineSegment(sketch, "E359", {"start": v(-1073.28, -543.02) * mm, "end": v(-1088.3, -566.03) * mm});
            skLineSegment(sketch, "E360", {"start": v(-1088.3, -566.03) * mm, "end": v(-1100.15, -587.32) * mm});
            skLineSegment(sketch, "E361", {"start": v(-1100.15, -587.32) * mm, "end": v(-1086.53, -608.3) * mm});
            skLineSegment(sketch, "E362", {"start": v(-1086.53, -608.3) * mm, "end": v(-1070.79, -627.73) * mm});
            skLineSegment(sketch, "E363", {"start": v(-1070.79, -627.73) * mm, "end": v(-1046.88, -623.03) * mm});
            skLineSegment(sketch, "E364", {"start": v(-1046.88, -623.03) * mm, "end": v(-1020.35, -615.87) * mm});
            skLineSegment(sketch, "E365", {"start": v(-1020.35, -615.87) * mm, "end": v(-998.62, -608.33) * mm});
            skLineSegment(sketch, "E366", {"start": v(-998.62, -608.33) * mm, "end": v(-981.58, -601.06) * mm});
            skLineSegment(sketch, "E367", {"start": v(-981.58, -601.06) * mm, "end": v(-969.07, -594.65) * mm});
            skLineSegment(sketch, "E368", {"start": v(-969.07, -594.65) * mm, "end": v(-956.46, -587.04) * mm});
            skLineSegment(sketch, "E369", {"start": v(-956.46, -587.04) * mm, "end": v(-946.96, -583.33) * mm});
            skLineSegment(sketch, "E370", {"start": v(-946.96, -583.33) * mm, "end": v(-940.63, -583.58) * mm});
            skLineSegment(sketch, "E371", {"start": v(-940.63, -583.58) * mm, "end": v(-901.93, -626.56) * mm});
            skLineSegment(sketch, "E372", {"start": v(-901.93, -626.56) * mm, "end": v(-902.35, -632.88) * mm});
            skLineSegment(sketch, "E373", {"start": v(-902.35, -632.88) * mm, "end": v(-907.03, -641.94) * mm});
            skLineSegment(sketch, "E374", {"start": v(-907.03, -641.94) * mm, "end": v(-915.92, -653.69) * mm});
            skLineSegment(sketch, "E375", {"start": v(-915.92, -653.69) * mm, "end": v(-923.6, -665.46) * mm});
            skLineSegment(sketch, "E376", {"start": v(-923.6, -665.46) * mm, "end": v(-932.61, -681.64) * mm});
            skLineSegment(sketch, "E377", {"start": v(-932.61, -681.64) * mm, "end": v(-942.38, -702.47) * mm});
            skLineSegment(sketch, "E378", {"start": v(-942.38, -702.47) * mm, "end": v(-952.28, -728.1) * mm});
            skLineSegment(sketch, "E379", {"start": v(-952.28, -728.1) * mm, "end": v(-959.45, -751.39) * mm});
            skLineSegment(sketch, "E380", {"start": v(-959.45, -751.39) * mm, "end": v(-941.76, -769.07) * mm});
            skLineSegment(sketch, "E381", {"start": v(-941.76, -769.07) * mm, "end": v(-922.32, -784.81) * mm});
            skLineSegment(sketch, "E382", {"start": v(-922.32, -784.81) * mm, "end": v(-899.92, -775.25) * mm});
            skLineSegment(sketch, "E383", {"start": v(-899.92, -775.25) * mm, "end": v(-875.46, -762.72) * mm});
            skLineSegment(sketch, "E384", {"start": v(-875.46, -762.72) * mm, "end": v(-855.77, -750.83) * mm});
            skLineSegment(sketch, "E385", {"start": v(-855.77, -750.83) * mm, "end": v(-840.61, -740.18) * mm});
            skLineSegment(sketch, "E386", {"start": v(-840.61, -740.18) * mm, "end": v(-829.71, -731.31) * mm});
            skLineSegment(sketch, "E387", {"start": v(-829.71, -731.31) * mm, "end": v(-818.95, -721.24) * mm});
            skLineSegment(sketch, "E388", {"start": v(-818.95, -721.24) * mm, "end": v(-810.44, -715.64) * mm});
            skLineSegment(sketch, "E389", {"start": v(-810.44, -715.64) * mm, "end": v(-804.2, -714.56) * mm});
            skLineSegment(sketch, "E390", {"start": v(-804.2, -714.56) * mm, "end": v(-757.4, -748.56) * mm});
            skLineSegment(sketch, "E391", {"start": v(-757.4, -748.56) * mm, "end": v(-756.5, -754.83) * mm});
            skLineSegment(sketch, "E392", {"start": v(-756.5, -754.83) * mm, "end": v(-759.19, -764.66) * mm});
            skLineSegment(sketch, "E393", {"start": v(-759.19, -764.66) * mm, "end": v(-765.44, -778) * mm});
            skLineSegment(sketch, "E394", {"start": v(-765.44, -778) * mm, "end": v(-770.5, -791.11) * mm});
            skLineSegment(sketch, "E395", {"start": v(-770.5, -791.11) * mm, "end": v(-775.96, -808.82) * mm});
            skLineSegment(sketch, "E396", {"start": v(-775.96, -808.82) * mm, "end": v(-781.18, -831.22) * mm});
            skLineSegment(sketch, "E397", {"start": v(-781.18, -831.22) * mm, "end": v(-785.53, -858.35) * mm});
            skLineSegment(sketch, "E398", {"start": v(-785.53, -858.35) * mm, "end": v(-787.7, -882.62) * mm});
            skLineSegment(sketch, "E399", {"start": v(-787.7, -882.62) * mm, "end": v(-766.73, -896.24) * mm});
            skLineSegment(sketch, "E400", {"start": v(-766.73, -896.24) * mm, "end": v(-744.44, -907.6) * mm});
            skLineSegment(sketch, "E401", {"start": v(-744.44, -907.6) * mm, "end": v(-724.52, -893.58) * mm});
            skLineSegment(sketch, "E402", {"start": v(-724.52, -893.58) * mm, "end": v(-703.2, -876.24) * mm});
            skLineSegment(sketch, "E403", {"start": v(-703.2, -876.24) * mm, "end": v(-686.4, -860.52) * mm});
            skLineSegment(sketch, "E404", {"start": v(-686.4, -860.52) * mm, "end": v(-673.8, -846.94) * mm});
            skLineSegment(sketch, "E405", {"start": v(-673.8, -846.94) * mm, "end": v(-664.98, -836) * mm});
            skLineSegment(sketch, "E406", {"start": v(-664.98, -836) * mm, "end": v(-656.55, -823.92) * mm});
            skLineSegment(sketch, "E407", {"start": v(-656.55, -823.92) * mm, "end": v(-649.38, -816.67) * mm});
            skLineSegment(sketch, "E408", {"start": v(-649.38, -816.67) * mm, "end": v(-643.5, -814.32) * mm});
            skLineSegment(sketch, "E409", {"start": v(-643.5, -814.32) * mm, "end": v(-590.66, -837.84) * mm});
            skLineSegment(sketch, "E410", {"start": v(-590.66, -837.84) * mm, "end": v(-588.47, -843.79) * mm});
            skLineSegment(sketch, "E411", {"start": v(-588.47, -843.79) * mm, "end": v(-589.06, -853.97) * mm});
            skLineSegment(sketch, "E412", {"start": v(-589.06, -853.97) * mm, "end": v(-592.4, -868.32) * mm});
            skLineSegment(sketch, "E413", {"start": v(-592.4, -868.32) * mm, "end": v(-594.63, -882.2) * mm});
            skLineSegment(sketch, "E414", {"start": v(-594.63, -882.2) * mm, "end": v(-596.29, -900.64) * mm});
            skLineSegment(sketch, "E415", {"start": v(-596.29, -900.64) * mm, "end": v(-596.74, -923.64) * mm});
            skLineSegment(sketch, "E416", {"start": v(-596.74, -923.64) * mm, "end": v(-595.35, -951.09) * mm});
            skLineSegment(sketch, "E417", {"start": v(-595.35, -951.09) * mm, "end": v(-592.43, -975.27) * mm});
            skLineSegment(sketch, "E418", {"start": v(-592.43, -975.27) * mm, "end": v(-569.08, -984.24) * mm});
            skLineSegment(sketch, "E419", {"start": v(-569.08, -984.24) * mm, "end": v(-544.92, -990.71) * mm});
            skLineSegment(sketch, "E420", {"start": v(-544.92, -990.71) * mm, "end": v(-528.35, -972.86) * mm});
            skLineSegment(sketch, "E421", {"start": v(-528.35, -972.86) * mm, "end": v(-511.1, -951.47) * mm});
            skLineSegment(sketch, "E422", {"start": v(-511.1, -951.47) * mm, "end": v(-497.94, -932.6) * mm});
            skLineSegment(sketch, "E423", {"start": v(-497.94, -932.6) * mm, "end": v(-488.43, -916.7) * mm});
            skLineSegment(sketch, "E424", {"start": v(-488.43, -916.7) * mm, "end": v(-482.08, -904.17) * mm});
            skLineSegment(sketch, "E425", {"start": v(-482.08, -904.17) * mm, "end": v(-476.35, -890.59) * mm});
            skLineSegment(sketch, "E426", {"start": v(-476.35, -890.59) * mm, "end": v(-470.85, -882) * mm});
            skLineSegment(sketch, "E427", {"start": v(-470.85, -882) * mm, "end": v(-465.58, -878.49) * mm});
            skLineSegment(sketch, "E428", {"start": v(-465.58, -878.49) * mm, "end": v(-409, -890.51) * mm});
            skLineSegment(sketch, "E429", {"start": v(-409, -890.51) * mm, "end": v(-405.62, -895.87) * mm});
            skLineSegment(sketch, "E430", {"start": v(-405.62, -895.87) * mm, "end": v(-404.09, -905.95) * mm});
            skLineSegment(sketch, "E431", {"start": v(-404.09, -905.95) * mm, "end": v(-404.38, -920.68) * mm});
            skLineSegment(sketch, "E432", {"start": v(-404.38, -920.68) * mm, "end": v(-403.67, -934.72) * mm});
            skLineSegment(sketch, "E433", {"start": v(-403.67, -934.72) * mm, "end": v(-401.45, -953.1) * mm});
            skLineSegment(sketch, "E434", {"start": v(-401.45, -953.1) * mm, "end": v(-397.1, -975.7) * mm});
            skLineSegment(sketch, "E435", {"start": v(-397.1, -975.7) * mm, "end": v(-390.05, -1002.25) * mm});
            skLineSegment(sketch, "E436", {"start": v(-390.05, -1002.25) * mm, "end": v(-382.16, -1025.3) * mm});
            skLineSegment(sketch, "E437", {"start": v(-382.16, -1025.3) * mm, "end": v(-357.46, -1029.22) * mm});
            skLineSegment(sketch, "E438", {"start": v(-357.46, -1029.22) * mm, "end": v(-332.48, -1030.53) * mm});
            skLineSegment(sketch, "E439", {"start": v(-332.48, -1030.53) * mm, "end": v(-319.98, -1009.62) * mm});
            skLineSegment(sketch, "E440", {"start": v(-319.98, -1009.62) * mm, "end": v(-307.55, -985.11) * mm});
            skLineSegment(sketch, "E441", {"start": v(-307.55, -985.11) * mm, "end": v(-298.6, -963.92) * mm});
            skLineSegment(sketch, "E442", {"start": v(-298.6, -963.92) * mm, "end": v(-292.61, -946.39) * mm});
            skLineSegment(sketch, "E443", {"start": v(-292.61, -946.39) * mm, "end": v(-289, -932.8) * mm});
            skLineSegment(sketch, "E444", {"start": v(-289, -932.8) * mm, "end": v(-286.22, -918.34) * mm});
            skLineSegment(sketch, "E445", {"start": v(-286.22, -918.34) * mm, "end": v(-282.62, -908.8) * mm});
            skLineSegment(sketch, "E446", {"start": v(-282.62, -908.8) * mm, "end": v(-278.2, -904.26) * mm});
            skLineSegment(sketch, "E447", {"start": v(-278.2, -904.26) * mm, "end": v(-220.37, -904.26) * mm});
            skLineSegment(sketch, "E448", {"start": v(-220.37, -904.26) * mm, "end": v(-215.95, -908.8) * mm});
            skLineSegment(sketch, "E449", {"start": v(-215.95, -908.8) * mm, "end": v(-212.35, -918.34) * mm});
            skLineSegment(sketch, "E450", {"start": v(-212.35, -918.34) * mm, "end": v(-209.57, -932.8) * mm});
            skLineSegment(sketch, "E451", {"start": v(-209.57, -932.8) * mm, "end": v(-205.96, -946.39) * mm});
            skLineSegment(sketch, "E452", {"start": v(-205.96, -946.39) * mm, "end": v(-199.96, -963.92) * mm});
            skLineSegment(sketch, "E453", {"start": v(-199.96, -963.92) * mm, "end": v(-191.02, -985.11) * mm});
            skLineSegment(sketch, "E454", {"start": v(-191.02, -985.11) * mm, "end": v(-178.6, -1009.62) * mm});
            skLineSegment(sketch, "E455", {"start": v(-178.6, -1009.62) * mm, "end": v(-166.09, -1030.53) * mm});
            skLineSegment(sketch, "E456", {"start": v(-166.09, -1030.53) * mm, "end": v(-141.11, -1029.22) * mm});
            skLineSegment(sketch, "E457", {"start": v(-141.11, -1029.22) * mm, "end": v(-116.4, -1025.3) * mm});
            skLineSegment(sketch, "E458", {"start": v(-116.4, -1025.3) * mm, "end": v(-108.52, -1002.25) * mm});
            skLineSegment(sketch, "E459", {"start": v(-108.52, -1002.25) * mm, "end": v(-101.46, -975.7) * mm});
            skLineSegment(sketch, "E460", {"start": v(-101.46, -975.7) * mm, "end": v(-97.12, -953.1) * mm});
            skLineSegment(sketch, "E461", {"start": v(-97.12, -953.1) * mm, "end": v(-94.9, -934.72) * mm});
            skLineSegment(sketch, "E462", {"start": v(-94.9, -934.72) * mm, "end": v(-94.2, -920.68) * mm});
            skLineSegment(sketch, "E463", {"start": v(-94.2, -920.68) * mm, "end": v(-94.48, -905.95) * mm});
            skLineSegment(sketch, "E464", {"start": v(-94.48, -905.95) * mm, "end": v(-92.95, -895.87) * mm});
            skLineSegment(sketch, "E465", {"start": v(-92.95, -895.87) * mm, "end": v(-89.57, -890.51) * mm});
            skLineSegment(sketch, "E466", {"start": v(-89.57, -890.51) * mm, "end": v(-33, -878.49) * mm});
            skLineSegment(sketch, "E467", {"start": v(-33, -878.49) * mm, "end": v(-27.73, -882) * mm});
            skLineSegment(sketch, "E468", {"start": v(-27.73, -882) * mm, "end": v(-22.22, -890.59) * mm});
            skLineSegment(sketch, "E469", {"start": v(-22.22, -890.59) * mm, "end": v(-16.5, -904.17) * mm});
            skLineSegment(sketch, "E470", {"start": v(-16.5, -904.17) * mm, "end": v(-10.14, -916.7) * mm});
            skLineSegment(sketch, "E471", {"start": v(-10.14, -916.7) * mm, "end": v(-0.63, -932.6) * mm});
            skLineSegment(sketch, "E472", {"start": v(-0.63, -932.6) * mm, "end": v(12.53, -951.47) * mm});
            skLineSegment(sketch, "E473", {"start": v(12.53, -951.47) * mm, "end": v(29.77, -972.86) * mm});
            skLineSegment(sketch, "E474", {"start": v(29.77, -972.86) * mm, "end": v(46.35, -990.71) * mm});
            skLineSegment(sketch, "E475", {"start": v(46.35, -990.71) * mm, "end": v(70.51, -984.24) * mm});
            skLineSegment(sketch, "E476", {"start": v(70.51, -984.24) * mm, "end": v(93.86, -975.27) * mm});
            skLineSegment(sketch, "E477", {"start": v(93.86, -975.27) * mm, "end": v(96.78, -951.09) * mm});
            skLineSegment(sketch, "E478", {"start": v(96.78, -951.09) * mm, "end": v(98.16, -923.64) * mm});
            skLineSegment(sketch, "E479", {"start": v(98.16, -923.64) * mm, "end": v(97.72, -900.64) * mm});
            skLineSegment(sketch, "E480", {"start": v(97.72, -900.64) * mm, "end": v(96.06, -882.2) * mm});
            skLineSegment(sketch, "E481", {"start": v(96.06, -882.2) * mm, "end": v(93.84, -868.32) * mm});
            skLineSegment(sketch, "E482", {"start": v(93.84, -868.32) * mm, "end": v(90.5, -853.97) * mm});
            skLineSegment(sketch, "E483", {"start": v(90.5, -853.97) * mm, "end": v(89.9, -843.79) * mm});
            skLineSegment(sketch, "E484", {"start": v(89.9, -843.79) * mm, "end": v(92.1, -837.84) * mm});
            skLineSegment(sketch, "E485", {"start": v(92.1, -837.84) * mm, "end": v(144.93, -814.32) * mm});
            skLineSegment(sketch, "E486", {"start": v(144.93, -814.32) * mm, "end": v(150.81, -816.67) * mm});
            skLineSegment(sketch, "E487", {"start": v(150.81, -816.67) * mm, "end": v(157.98, -823.92) * mm});
            skLineSegment(sketch, "E488", {"start": v(157.98, -823.92) * mm, "end": v(166.4, -836) * mm});
            skLineSegment(sketch, "E489", {"start": v(166.4, -836) * mm, "end": v(175.23, -846.94) * mm});
            skLineSegment(sketch, "E490", {"start": v(175.23, -846.94) * mm, "end": v(187.83, -860.52) * mm});
            skLineSegment(sketch, "E491", {"start": v(187.83, -860.52) * mm, "end": v(204.63, -876.24) * mm});
            skLineSegment(sketch, "E492", {"start": v(204.63, -876.24) * mm, "end": v(225.94, -893.58) * mm});
            skLineSegment(sketch, "E493", {"start": v(225.94, -893.58) * mm, "end": v(245.87, -907.6) * mm});
            skLineSegment(sketch, "E494", {"start": v(245.87, -907.6) * mm, "end": v(268.16, -896.24) * mm});
            skLineSegment(sketch, "E495", {"start": v(268.16, -896.24) * mm, "end": v(289.14, -882.62) * mm});
            skLineSegment(sketch, "E496", {"start": v(289.14, -882.62) * mm, "end": v(286.96, -858.35) * mm});
            skLineSegment(sketch, "E497", {"start": v(286.96, -858.35) * mm, "end": v(282.6, -831.22) * mm});
            skLineSegment(sketch, "E498", {"start": v(282.6, -831.22) * mm, "end": v(277.39, -808.82) * mm});
            skLineSegment(sketch, "E499", {"start": v(277.39, -808.82) * mm, "end": v(271.93, -791.11) * mm});
            skLineSegment(sketch, "E500", {"start": v(271.93, -791.11) * mm, "end": v(266.87, -778) * mm});
            skLineSegment(sketch, "E501", {"start": v(266.87, -778) * mm, "end": v(260.62, -764.66) * mm});
            skLineSegment(sketch, "E502", {"start": v(260.62, -764.66) * mm, "end": v(257.92, -754.83) * mm});
            skLineSegment(sketch, "E503", {"start": v(257.92, -754.83) * mm, "end": v(258.83, -748.56) * mm});
            skLineSegment(sketch, "E504", {"start": v(258.83, -748.56) * mm, "end": v(305.62, -714.56) * mm});
            skLineSegment(sketch, "E505", {"start": v(305.62, -714.56) * mm, "end": v(311.86, -715.64) * mm});
            skLineSegment(sketch, "E506", {"start": v(311.86, -715.64) * mm, "end": v(320.38, -721.24) * mm});
            skLineSegment(sketch, "E507", {"start": v(320.38, -721.24) * mm, "end": v(331.14, -731.31) * mm});
            skLineSegment(sketch, "E508", {"start": v(331.14, -731.31) * mm, "end": v(342.04, -740.18) * mm});
            skLineSegment(sketch, "E509", {"start": v(342.04, -740.18) * mm, "end": v(357.2, -750.83) * mm});
            skLineSegment(sketch, "E510", {"start": v(357.2, -750.83) * mm, "end": v(376.89, -762.72) * mm});
            skLineSegment(sketch, "E511", {"start": v(376.89, -762.72) * mm, "end": v(401.35, -775.25) * mm});
            skLineSegment(sketch, "E512", {"start": v(401.35, -775.25) * mm, "end": v(423.75, -784.81) * mm});
            skLineSegment(sketch, "E513", {"start": v(423.75, -784.81) * mm, "end": v(443.2, -769.07) * mm});
            skLineSegment(sketch, "E514", {"start": v(443.2, -769.07) * mm, "end": v(460.88, -751.39) * mm});
            skLineSegment(sketch, "E515", {"start": v(460.88, -751.39) * mm, "end": v(453.7, -728.1) * mm});
            skLineSegment(sketch, "E516", {"start": v(453.7, -728.1) * mm, "end": v(443.8, -702.47) * mm});
            skLineSegment(sketch, "E517", {"start": v(443.8, -702.47) * mm, "end": v(434.04, -681.64) * mm});
            skLineSegment(sketch, "E518", {"start": v(434.04, -681.64) * mm, "end": v(425.03, -665.46) * mm});
            skLineSegment(sketch, "E519", {"start": v(425.03, -665.46) * mm, "end": v(417.35, -653.69) * mm});
            skLineSegment(sketch, "E520", {"start": v(417.35, -653.69) * mm, "end": v(408.45, -641.94) * mm});
            skLineSegment(sketch, "E521", {"start": v(408.45, -641.94) * mm, "end": v(403.77, -632.88) * mm});
            skLineSegment(sketch, "E522", {"start": v(403.77, -632.88) * mm, "end": v(403.36, -626.56) * mm});
            skLineSegment(sketch, "E523", {"start": v(403.36, -626.56) * mm, "end": v(442.06, -583.58) * mm});
            skLineSegment(sketch, "E524", {"start": v(442.06, -583.58) * mm, "end": v(448.4, -583.33) * mm});
            skLineSegment(sketch, "E525", {"start": v(448.4, -583.33) * mm, "end": v(457.89, -587.04) * mm});
            skLineSegment(sketch, "E526", {"start": v(457.89, -587.04) * mm, "end": v(470.5, -594.65) * mm});
            skLineSegment(sketch, "E527", {"start": v(470.5, -594.65) * mm, "end": v(483.01, -601.06) * mm});
            skLineSegment(sketch, "E528", {"start": v(483.01, -601.06) * mm, "end": v(500.05, -608.33) * mm});
            skLineSegment(sketch, "E529", {"start": v(500.05, -608.33) * mm, "end": v(521.78, -615.87) * mm});
            skLineSegment(sketch, "E530", {"start": v(521.78, -615.87) * mm, "end": v(548.31, -623.03) * mm});
            skLineSegment(sketch, "E531", {"start": v(548.31, -623.03) * mm, "end": v(572.22, -627.73) * mm});
            skLineSegment(sketch, "E532", {"start": v(572.22, -627.73) * mm, "end": v(587.96, -608.3) * mm});
            skLineSegment(sketch, "E533", {"start": v(587.96, -608.3) * mm, "end": v(601.58, -587.32) * mm});
            skLineSegment(sketch, "E534", {"start": v(601.58, -587.32) * mm, "end": v(589.72, -566.03) * mm});
            skLineSegment(sketch, "E535", {"start": v(589.72, -566.03) * mm, "end": v(574.71, -543.02) * mm});
            skLineSegment(sketch, "E536", {"start": v(574.71, -543.02) * mm, "end": v(560.83, -524.67) * mm});
            skLineSegment(sketch, "E537", {"start": v(560.83, -524.67) * mm, "end": v(548.65, -510.72) * mm});
            skLineSegment(sketch, "E538", {"start": v(548.65, -510.72) * mm, "end": v(538.7, -500.8) * mm});
            skLineSegment(sketch, "E539", {"start": v(538.7, -500.8) * mm, "end": v(527.55, -491.16) * mm});
            skLineSegment(sketch, "E540", {"start": v(527.55, -491.16) * mm, "end": v(521.09, -483.27) * mm});
            skLineSegment(sketch, "E541", {"start": v(521.09, -483.27) * mm, "end": v(519.37, -477.17) * mm});
            skLineSegment(sketch, "E542", {"start": v(519.37, -477.17) * mm, "end": v(548.28, -427.08) * mm});
            skLineSegment(sketch, "E543", {"start": v(548.28, -427.08) * mm, "end": v(554.43, -425.53) * mm});
            skLineSegment(sketch, "E544", {"start": v(554.43, -425.53) * mm, "end": v(564.49, -427.18) * mm});
            skLineSegment(sketch, "E545", {"start": v(564.49, -427.18) * mm, "end": v(578.41, -432) * mm});
            skLineSegment(sketch, "E546", {"start": v(578.41, -432) * mm, "end": v(591.97, -435.67) * mm});
            skLineSegment(sketch, "E547", {"start": v(591.97, -435.67) * mm, "end": v(610.15, -439.24) * mm});
            skLineSegment(sketch, "E548", {"start": v(610.15, -439.24) * mm, "end": v(632.98, -442.1) * mm});
            skLineSegment(sketch, "E549", {"start": v(632.98, -442.1) * mm, "end": v(660.42, -443.59) * mm});
            skLineSegment(sketch, "E550", {"start": v(660.42, -443.59) * mm, "end": v(684.78, -443.21) * mm});
            skLineSegment(sketch, "E551", {"start": v(684.78, -443.21) * mm, "end": v(696.13, -420.93) * mm});
            skLineSegment(sketch, "E552", {"start": v(696.13, -420.93) * mm, "end": v(705.1, -397.58) * mm});
            skLineSegment(sketch, "E553", {"start": v(705.1, -397.58) * mm, "end": v(689.07, -379.22) * mm});
            skLineSegment(sketch, "E554", {"start": v(689.07, -379.22) * mm, "end": v(669.6, -359.83) * mm});
            skLineSegment(sketch, "E555", {"start": v(669.6, -359.83) * mm, "end": v(652.21, -344.78) * mm});
            skLineSegment(sketch, "E556", {"start": v(652.21, -344.78) * mm, "end": v(637.4, -333.66) * mm});
            skLineSegment(sketch, "E557", {"start": v(637.4, -333.66) * mm, "end": v(625.6, -326.03) * mm});
            skLineSegment(sketch, "E558", {"start": v(625.6, -326.03) * mm, "end": v(612.69, -318.91) * mm});
            skLineSegment(sketch, "E559", {"start": v(612.69, -318.91) * mm, "end": v(604.73, -312.54) * mm});
            skLineSegment(sketch, "E560", {"start": v(604.73, -312.54) * mm, "end": v(601.78, -306.93) * mm});
            skLineSegment(sketch, "E561", {"start": v(601.78, -306.93) * mm, "end": v(619.65, -251.93) * mm});
            skLineSegment(sketch, "E562", {"start": v(619.65, -251.93) * mm, "end": v(625.33, -249.13) * mm});
            skLineSegment(sketch, "E563", {"start": v(625.33, -249.13) * mm, "end": v(635.52, -248.65) * mm});
            skLineSegment(sketch, "E564", {"start": v(635.52, -248.65) * mm, "end": v(650.14, -250.48) * mm});
            skLineSegment(sketch, "E565", {"start": v(650.14, -250.48) * mm, "end": v(664.17, -251.24) * mm});
            skLineSegment(sketch, "E566", {"start": v(664.17, -251.24) * mm, "end": v(682.7, -250.96) * mm});
            skLineSegment(sketch, "E567", {"start": v(682.7, -250.96) * mm, "end": v(705.62, -249) * mm});
            skLineSegment(sketch, "E568", {"start": v(705.62, -249) * mm, "end": v(732.77, -244.76) * mm});
            skLineSegment(sketch, "E569", {"start": v(732.77, -244.76) * mm, "end": v(756.52, -239.33) * mm});
            skLineSegment(sketch, "E570", {"start": v(-238.72, -49.69) * mm, "end": v(-249.29, -50.8) * mm});
            skLineSegment(sketch, "E571", {"start": v(-249.29, -50.8) * mm, "end": v(-259.85, -49.69) * mm});
            skLineSegment(sketch, "E572", {"start": v(-259.85, -49.69) * mm, "end": v(-269.95, -46.4) * mm});
            skLineSegment(sketch, "E573", {"start": v(-269.95, -46.4) * mm, "end": v(-279.15, -41.1) * mm});
            skLineSegment(sketch, "E574", {"start": v(-279.15, -41.1) * mm, "end": v(-287.04, -34) * mm});
            skLineSegment(sketch, "E575", {"start": v(-287.04, -34) * mm, "end": v(-293.28, -25.4) * mm});
            skLineSegment(sketch, "E576", {"start": v(-293.28, -25.4) * mm, "end": v(-297.6, -15.7) * mm});
            skLineSegment(sketch, "E577", {"start": v(-297.6, -15.7) * mm, "end": v(-299.8, -5.31) * mm});
            skLineSegment(sketch, "E578", {"start": v(-299.8, -5.31) * mm, "end": v(-299.8, 5.31) * mm});
            skLineSegment(sketch, "E579", {"start": v(-299.8, 5.31) * mm, "end": v(-297.6, 15.7) * mm});
            skLineSegment(sketch, "E580", {"start": v(-297.6, 15.7) * mm, "end": v(-293.28, 25.4) * mm});
            skLineSegment(sketch, "E581", {"start": v(-293.28, 25.4) * mm, "end": v(-287.04, 34) * mm});
            skLineSegment(sketch, "E582", {"start": v(-287.04, 34) * mm, "end": v(-279.15, 41.1) * mm});
            skLineSegment(sketch, "E583", {"start": v(-279.15, 41.1) * mm, "end": v(-269.95, 46.4) * mm});
            skLineSegment(sketch, "E584", {"start": v(-269.95, 46.4) * mm, "end": v(-259.85, 49.69) * mm});
            skLineSegment(sketch, "E585", {"start": v(-259.85, 49.69) * mm, "end": v(-249.29, 50.8) * mm});
            skLineSegment(sketch, "E586", {"start": v(-249.29, 50.8) * mm, "end": v(-238.72, 49.69) * mm});
            skLineSegment(sketch, "E587", {"start": v(-238.72, 49.69) * mm, "end": v(-228.62, 46.4) * mm});
            skLineSegment(sketch, "E588", {"start": v(-228.62, 46.4) * mm, "end": v(-219.43, 41.1) * mm});
            skLineSegment(sketch, "E589", {"start": v(-219.43, 41.1) * mm, "end": v(-211.53, 34) * mm});
            skLineSegment(sketch, "E590", {"start": v(-211.53, 34) * mm, "end": v(-205.3, 25.4) * mm});
            skLineSegment(sketch, "E591", {"start": v(-205.3, 25.4) * mm, "end": v(-200.97, 15.7) * mm});
            skLineSegment(sketch, "E592", {"start": v(-200.97, 15.7) * mm, "end": v(-198.76, 5.31) * mm});
            skLineSegment(sketch, "E593", {"start": v(-198.76, 5.31) * mm, "end": v(-198.76, -5.31) * mm});
            skLineSegment(sketch, "E594", {"start": v(-198.76, -5.31) * mm, "end": v(-200.97, -15.7) * mm});
            skLineSegment(sketch, "E595", {"start": v(-200.97, -15.7) * mm, "end": v(-205.3, -25.4) * mm});
            skLineSegment(sketch, "E596", {"start": v(-205.3, -25.4) * mm, "end": v(-211.53, -34) * mm});
            skLineSegment(sketch, "E597", {"start": v(-211.53, -34) * mm, "end": v(-219.43, -41.1) * mm});
            skLineSegment(sketch, "E598", {"start": v(-219.43, -41.1) * mm, "end": v(-228.62, -46.4) * mm});
            skLineSegment(sketch, "E599", {"start": v(-228.62, -46.4) * mm, "end": v(-238.72, -49.69) * mm});
            skSolve(sketch);
        }
        {
            var Q0;
            Q0=makeQuery(id+"F0.imprint","IMPRINT",FACE,{"disambiguationData":[TD([[makeQuery(id+"F0.imprint","IMPRINT",EDGE,{"derivedFrom":sQuery(id+"F0.wireOp",EDGE,"E0")}),1.0]])]});
            extrude(context, id + "F1", {"entities" : qUnion([Q0]), "depth" : 127 * mm, "offsetDistance" : 25.4 * mm});
        }
        {
            var Q0;
            Q0=makeQuery(id+"F1.opExtrude","SWEPT_BODY",BODY,{"disambiguationData":[OSD([sQuery(id+"F0.wireOp",EDGE,"E0"),sQuery(id+"F0.wireOp",EDGE,"E1"),sQuery(id+"F0.wireOp",EDGE,"E2"),sQuery(id+"F0.wireOp",EDGE,"E3"),sQuery(id+"F0.wireOp",EDGE,"E4"),sQuery(id+"F0.wireOp",EDGE,"E5"),sQuery(id+"F0.wireOp",EDGE,"E6"),sQuery(id+"F0.wireOp",EDGE,"E7"),sQuery(id+"F0.wireOp",EDGE,"E8"),sQuery(id+"F0.wireOp",EDGE,"E9"),sQuery(id+"F0.wireOp",EDGE,"E10"),sQuery(id+"F0.wireOp",EDGE,"E11"),sQuery(id+"F0.wireOp",EDGE,"E12"),sQuery(id+"F0.wireOp",EDGE,"E13"),sQuery(id+"F0.wireOp",EDGE,"E14"),sQuery(id+"F0.wireOp",EDGE,"E15"),sQuery(id+"F0.wireOp",EDGE,"E16"),sQuery(id+"F0.wireOp",EDGE,"E17"),sQuery(id+"F0.wireOp",EDGE,"E18"),sQuery(id+"F0.wireOp",EDGE,"E19"),sQuery(id+"F0.wireOp",EDGE,"E20"),sQuery(id+"F0.wireOp",EDGE,"E21"),sQuery(id+"F0.wireOp",EDGE,"E22"),sQuery(id+"F0.wireOp",EDGE,"E23"),sQuery(id+"F0.wireOp",EDGE,"E24"),sQuery(id+"F0.wireOp",EDGE,"E25"),sQuery(id+"F0.wireOp",EDGE,"E26"),sQuery(id+"F0.wireOp",EDGE,"E27"),sQuery(id+"F0.wireOp",EDGE,"E28"),sQuery(id+"F0.wireOp",EDGE,"E29"),sQuery(id+"F0.wireOp",EDGE,"E30"),sQuery(id+"F0.wireOp",EDGE,"E31"),sQuery(id+"F0.wireOp",EDGE,"E32"),sQuery(id+"F0.wireOp",EDGE,"E33"),sQuery(id+"F0.wireOp",EDGE,"E34"),sQuery(id+"F0.wireOp",EDGE,"E35"),sQuery(id+"F0.wireOp",EDGE,"E36"),sQuery(id+"F0.wireOp",EDGE,"E37"),sQuery(id+"F0.wireOp",EDGE,"E38"),sQuery(id+"F0.wireOp",EDGE,"E39"),sQuery(id+"F0.wireOp",EDGE,"E40"),sQuery(id+"F0.wireOp",EDGE,"E41"),sQuery(id+"F0.wireOp",EDGE,"E42"),sQuery(id+"F0.wireOp",EDGE,"E43"),sQuery(id+"F0.wireOp",EDGE,"E44"),sQuery(id+"F0.wireOp",EDGE,"E45"),sQuery(id+"F0.wireOp",EDGE,"E46"),sQuery(id+"F0.wireOp",EDGE,"E47"),sQuery(id+"F0.wireOp",EDGE,"E48"),sQuery(id+"F0.wireOp",EDGE,"E49"),sQuery(id+"F0.wireOp",EDGE,"E50"),sQuery(id+"F0.wireOp",EDGE,"E51"),sQuery(id+"F0.wireOp",EDGE,"E52"),sQuery(id+"F0.wireOp",EDGE,"E53"),sQuery(id+"F0.wireOp",EDGE,"E54"),sQuery(id+"F0.wireOp",EDGE,"E55"),sQuery(id+"F0.wireOp",EDGE,"E56"),sQuery(id+"F0.wireOp",EDGE,"E57"),sQuery(id+"F0.wireOp",EDGE,"E58"),sQuery(id+"F0.wireOp",EDGE,"E59"),sQuery(id+"F0.wireOp",EDGE,"E60"),sQuery(id+"F0.wireOp",EDGE,"E61"),sQuery(id+"F0.wireOp",EDGE,"E62"),sQuery(id+"F0.wireOp",EDGE,"E63"),sQuery(id+"F0.wireOp",EDGE,"E64"),sQuery(id+"F0.wireOp",EDGE,"E65"),sQuery(id+"F0.wireOp",EDGE,"E66"),sQuery(id+"F0.wireOp",EDGE,"E67"),sQuery(id+"F0.wireOp",EDGE,"E68"),sQuery(id+"F0.wireOp",EDGE,"E69"),sQuery(id+"F0.wireOp",EDGE,"E70"),sQuery(id+"F0.wireOp",EDGE,"E71"),sQuery(id+"F0.wireOp",EDGE,"E72"),sQuery(id+"F0.wireOp",EDGE,"E73"),sQuery(id+"F0.wireOp",EDGE,"E74"),sQuery(id+"F0.wireOp",EDGE,"E75"),sQuery(id+"F0.wireOp",EDGE,"E76"),sQuery(id+"F0.wireOp",EDGE,"E77"),sQuery(id+"F0.wireOp",EDGE,"E78"),sQuery(id+"F0.wireOp",EDGE,"E79"),sQuery(id+"F0.wireOp",EDGE,"E80"),sQuery(id+"F0.wireOp",EDGE,"E81"),sQuery(id+"F0.wireOp",EDGE,"E82"),sQuery(id+"F0.wireOp",EDGE,"E83"),sQuery(id+"F0.wireOp",EDGE,"E84"),sQuery(id+"F0.wireOp",EDGE,"E85"),sQuery(id+"F0.wireOp",EDGE,"E86"),sQuery(id+"F0.wireOp",EDGE,"E87"),sQuery(id+"F0.wireOp",EDGE,"E88"),sQuery(id+"F0.wireOp",EDGE,"E89"),sQuery(id+"F0.wireOp",EDGE,"E90"),sQuery(id+"F0.wireOp",EDGE,"E91"),sQuery(id+"F0.wireOp",EDGE,"E92"),sQuery(id+"F0.wireOp",EDGE,"E93"),sQuery(id+"F0.wireOp",EDGE,"E94"),sQuery(id+"F0.wireOp",EDGE,"E95"),sQuery(id+"F0.wireOp",EDGE,"E96"),sQuery(id+"F0.wireOp",EDGE,"E97"),sQuery(id+"F0.wireOp",EDGE,"E98"),sQuery(id+"F0.wireOp",EDGE,"E99"),sQuery(id+"F0.wireOp",EDGE,"E100"),sQuery(id+"F0.wireOp",EDGE,"E101"),sQuery(id+"F0.wireOp",EDGE,"E102"),sQuery(id+"F0.wireOp",EDGE,"E103"),sQuery(id+"F0.wireOp",EDGE,"E104"),sQuery(id+"F0.wireOp",EDGE,"E105"),sQuery(id+"F0.wireOp",EDGE,"E106"),sQuery(id+"F0.wireOp",EDGE,"E107"),sQuery(id+"F0.wireOp",EDGE,"E108"),sQuery(id+"F0.wireOp",EDGE,"E109"),sQuery(id+"F0.wireOp",EDGE,"E110"),sQuery(id+"F0.wireOp",EDGE,"E111"),sQuery(id+"F0.wireOp",EDGE,"E112"),sQuery(id+"F0.wireOp",EDGE,"E113"),sQuery(id+"F0.wireOp",EDGE,"E114"),sQuery(id+"F0.wireOp",EDGE,"E115"),sQuery(id+"F0.wireOp",EDGE,"E116"),sQuery(id+"F0.wireOp",EDGE,"E117"),sQuery(id+"F0.wireOp",EDGE,"E118"),sQuery(id+"F0.wireOp",EDGE,"E119"),sQuery(id+"F0.wireOp",EDGE,"E120"),sQuery(id+"F0.wireOp",EDGE,"E121"),sQuery(id+"F0.wireOp",EDGE,"E122"),sQuery(id+"F0.wireOp",EDGE,"E123"),sQuery(id+"F0.wireOp",EDGE,"E124"),sQuery(id+"F0.wireOp",EDGE,"E125"),sQuery(id+"F0.wireOp",EDGE,"E126"),sQuery(id+"F0.wireOp",EDGE,"E127"),sQuery(id+"F0.wireOp",EDGE,"E128"),sQuery(id+"F0.wireOp",EDGE,"E129"),sQuery(id+"F0.wireOp",EDGE,"E130"),sQuery(id+"F0.wireOp",EDGE,"E131"),sQuery(id+"F0.wireOp",EDGE,"E132"),sQuery(id+"F0.wireOp",EDGE,"E133"),sQuery(id+"F0.wireOp",EDGE,"E134"),sQuery(id+"F0.wireOp",EDGE,"E135"),sQuery(id+"F0.wireOp",EDGE,"E136"),sQuery(id+"F0.wireOp",EDGE,"E137"),sQuery(id+"F0.wireOp",EDGE,"E138"),sQuery(id+"F0.wireOp",EDGE,"E139"),sQuery(id+"F0.wireOp",EDGE,"E140"),sQuery(id+"F0.wireOp",EDGE,"E141"),sQuery(id+"F0.wireOp",EDGE,"E142"),sQuery(id+"F0.wireOp",EDGE,"E143"),sQuery(id+"F0.wireOp",EDGE,"E144"),sQuery(id+"F0.wireOp",EDGE,"E145"),sQuery(id+"F0.wireOp",EDGE,"E146"),sQuery(id+"F0.wireOp",EDGE,"E147"),sQuery(id+"F0.wireOp",EDGE,"E148"),sQuery(id+"F0.wireOp",EDGE,"E149"),sQuery(id+"F0.wireOp",EDGE,"E150"),sQuery(id+"F0.wireOp",EDGE,"E151"),sQuery(id+"F0.wireOp",EDGE,"E152"),sQuery(id+"F0.wireOp",EDGE,"E153"),sQuery(id+"F0.wireOp",EDGE,"E154"),sQuery(id+"F0.wireOp",EDGE,"E155"),sQuery(id+"F0.wireOp",EDGE,"E156"),sQuery(id+"F0.wireOp",EDGE,"E157"),sQuery(id+"F0.wireOp",EDGE,"E158"),sQuery(id+"F0.wireOp",EDGE,"E159"),sQuery(id+"F0.wireOp",EDGE,"E160"),sQuery(id+"F0.wireOp",EDGE,"E161"),sQuery(id+"F0.wireOp",EDGE,"E162"),sQuery(id+"F0.wireOp",EDGE,"E163"),sQuery(id+"F0.wireOp",EDGE,"E164"),sQuery(id+"F0.wireOp",EDGE,"E165"),sQuery(id+"F0.wireOp",EDGE,"E166"),sQuery(id+"F0.wireOp",EDGE,"E167"),sQuery(id+"F0.wireOp",EDGE,"E168"),sQuery(id+"F0.wireOp",EDGE,"E169"),sQuery(id+"F0.wireOp",EDGE,"E170"),sQuery(id+"F0.wireOp",EDGE,"E171"),sQuery(id+"F0.wireOp",EDGE,"E172"),sQuery(id+"F0.wireOp",EDGE,"E173"),sQuery(id+"F0.wireOp",EDGE,"E174"),sQuery(id+"F0.wireOp",EDGE,"E175"),sQuery(id+"F0.wireOp",EDGE,"E176"),sQuery(id+"F0.wireOp",EDGE,"E177"),sQuery(id+"F0.wireOp",EDGE,"E178"),sQuery(id+"F0.wireOp",EDGE,"E179"),sQuery(id+"F0.wireOp",EDGE,"E180"),sQuery(id+"F0.wireOp",EDGE,"E181"),sQuery(id+"F0.wireOp",EDGE,"E182"),sQuery(id+"F0.wireOp",EDGE,"E183"),sQuery(id+"F0.wireOp",EDGE,"E184"),sQuery(id+"F0.wireOp",EDGE,"E185"),sQuery(id+"F0.wireOp",EDGE,"E186"),sQuery(id+"F0.wireOp",EDGE,"E187"),sQuery(id+"F0.wireOp",EDGE,"E188"),sQuery(id+"F0.wireOp",EDGE,"E189"),sQuery(id+"F0.wireOp",EDGE,"E190"),sQuery(id+"F0.wireOp",EDGE,"E191"),sQuery(id+"F0.wireOp",EDGE,"E192"),sQuery(id+"F0.wireOp",EDGE,"E193"),sQuery(id+"F0.wireOp",EDGE,"E194"),sQuery(id+"F0.wireOp",EDGE,"E195"),sQuery(id+"F0.wireOp",EDGE,"E196"),sQuery(id+"F0.wireOp",EDGE,"E197"),sQuery(id+"F0.wireOp",EDGE,"E198"),sQuery(id+"F0.wireOp",EDGE,"E199"),sQuery(id+"F0.wireOp",EDGE,"E200"),sQuery(id+"F0.wireOp",EDGE,"E201"),sQuery(id+"F0.wireOp",EDGE,"E202"),sQuery(id+"F0.wireOp",EDGE,"E203"),sQuery(id+"F0.wireOp",EDGE,"E204"),sQuery(id+"F0.wireOp",EDGE,"E205"),sQuery(id+"F0.wireOp",EDGE,"E206"),sQuery(id+"F0.wireOp",EDGE,"E207"),sQuery(id+"F0.wireOp",EDGE,"E208"),sQuery(id+"F0.wireOp",EDGE,"E209"),sQuery(id+"F0.wireOp",EDGE,"E210"),sQuery(id+"F0.wireOp",EDGE,"E211"),sQuery(id+"F0.wireOp",EDGE,"E212"),sQuery(id+"F0.wireOp",EDGE,"E213"),sQuery(id+"F0.wireOp",EDGE,"E214"),sQuery(id+"F0.wireOp",EDGE,"E215"),sQuery(id+"F0.wireOp",EDGE,"E216"),sQuery(id+"F0.wireOp",EDGE,"E217"),sQuery(id+"F0.wireOp",EDGE,"E218"),sQuery(id+"F0.wireOp",EDGE,"E219"),sQuery(id+"F0.wireOp",EDGE,"E220"),sQuery(id+"F0.wireOp",EDGE,"E221"),sQuery(id+"F0.wireOp",EDGE,"E222"),sQuery(id+"F0.wireOp",EDGE,"E223"),sQuery(id+"F0.wireOp",EDGE,"E224"),sQuery(id+"F0.wireOp",EDGE,"E225"),sQuery(id+"F0.wireOp",EDGE,"E226"),sQuery(id+"F0.wireOp",EDGE,"E227"),sQuery(id+"F0.wireOp",EDGE,"E228"),sQuery(id+"F0.wireOp",EDGE,"E229"),sQuery(id+"F0.wireOp",EDGE,"E230"),sQuery(id+"F0.wireOp",EDGE,"E231"),sQuery(id+"F0.wireOp",EDGE,"E232"),sQuery(id+"F0.wireOp",EDGE,"E233"),sQuery(id+"F0.wireOp",EDGE,"E234"),sQuery(id+"F0.wireOp",EDGE,"E235"),sQuery(id+"F0.wireOp",EDGE,"E236"),sQuery(id+"F0.wireOp",EDGE,"E237"),sQuery(id+"F0.wireOp",EDGE,"E238"),sQuery(id+"F0.wireOp",EDGE,"E239"),sQuery(id+"F0.wireOp",EDGE,"E240"),sQuery(id+"F0.wireOp",EDGE,"E241"),sQuery(id+"F0.wireOp",EDGE,"E242"),sQuery(id+"F0.wireOp",EDGE,"E243"),sQuery(id+"F0.wireOp",EDGE,"E244"),sQuery(id+"F0.wireOp",EDGE,"E245"),sQuery(id+"F0.wireOp",EDGE,"E246"),sQuery(id+"F0.wireOp",EDGE,"E247"),sQuery(id+"F0.wireOp",EDGE,"E248"),sQuery(id+"F0.wireOp",EDGE,"E249"),sQuery(id+"F0.wireOp",EDGE,"E250"),sQuery(id+"F0.wireOp",EDGE,"E251"),sQuery(id+"F0.wireOp",EDGE,"E252"),sQuery(id+"F0.wireOp",EDGE,"E253"),sQuery(id+"F0.wireOp",EDGE,"E254"),sQuery(id+"F0.wireOp",EDGE,"E255"),sQuery(id+"F0.wireOp",EDGE,"E256"),sQuery(id+"F0.wireOp",EDGE,"E257"),sQuery(id+"F0.wireOp",EDGE,"E258"),sQuery(id+"F0.wireOp",EDGE,"E259"),sQuery(id+"F0.wireOp",EDGE,"E260"),sQuery(id+"F0.wireOp",EDGE,"E261"),sQuery(id+"F0.wireOp",EDGE,"E262"),sQuery(id+"F0.wireOp",EDGE,"E263"),sQuery(id+"F0.wireOp",EDGE,"E264"),sQuery(id+"F0.wireOp",EDGE,"E265"),sQuery(id+"F0.wireOp",EDGE,"E266"),sQuery(id+"F0.wireOp",EDGE,"E267"),sQuery(id+"F0.wireOp",EDGE,"E268"),sQuery(id+"F0.wireOp",EDGE,"E269"),sQuery(id+"F0.wireOp",EDGE,"E270"),sQuery(id+"F0.wireOp",EDGE,"E271"),sQuery(id+"F0.wireOp",EDGE,"E272"),sQuery(id+"F0.wireOp",EDGE,"E273"),sQuery(id+"F0.wireOp",EDGE,"E274"),sQuery(id+"F0.wireOp",EDGE,"E275"),sQuery(id+"F0.wireOp",EDGE,"E276"),sQuery(id+"F0.wireOp",EDGE,"E277"),sQuery(id+"F0.wireOp",EDGE,"E278"),sQuery(id+"F0.wireOp",EDGE,"E279"),sQuery(id+"F0.wireOp",EDGE,"E280"),sQuery(id+"F0.wireOp",EDGE,"E281"),sQuery(id+"F0.wireOp",EDGE,"E282"),sQuery(id+"F0.wireOp",EDGE,"E283"),sQuery(id+"F0.wireOp",EDGE,"E284"),sQuery(id+"F0.wireOp",EDGE,"E285"),sQuery(id+"F0.wireOp",EDGE,"E286"),sQuery(id+"F0.wireOp",EDGE,"E287"),sQuery(id+"F0.wireOp",EDGE,"E288"),sQuery(id+"F0.wireOp",EDGE,"E289"),sQuery(id+"F0.wireOp",EDGE,"E290"),sQuery(id+"F0.wireOp",EDGE,"E291"),sQuery(id+"F0.wireOp",EDGE,"E292"),sQuery(id+"F0.wireOp",EDGE,"E293"),sQuery(id+"F0.wireOp",EDGE,"E294"),sQuery(id+"F0.wireOp",EDGE,"E295"),sQuery(id+"F0.wireOp",EDGE,"E296"),sQuery(id+"F0.wireOp",EDGE,"E297"),sQuery(id+"F0.wireOp",EDGE,"E298"),sQuery(id+"F0.wireOp",EDGE,"E299"),sQuery(id+"F0.wireOp",EDGE,"E300"),sQuery(id+"F0.wireOp",EDGE,"E301"),sQuery(id+"F0.wireOp",EDGE,"E302"),sQuery(id+"F0.wireOp",EDGE,"E303"),sQuery(id+"F0.wireOp",EDGE,"E304"),sQuery(id+"F0.wireOp",EDGE,"E305"),sQuery(id+"F0.wireOp",EDGE,"E306"),sQuery(id+"F0.wireOp",EDGE,"E307"),sQuery(id+"F0.wireOp",EDGE,"E308"),sQuery(id+"F0.wireOp",EDGE,"E309"),sQuery(id+"F0.wireOp",EDGE,"E310"),sQuery(id+"F0.wireOp",EDGE,"E311"),sQuery(id+"F0.wireOp",EDGE,"E312"),sQuery(id+"F0.wireOp",EDGE,"E313"),sQuery(id+"F0.wireOp",EDGE,"E314"),sQuery(id+"F0.wireOp",EDGE,"E315"),sQuery(id+"F0.wireOp",EDGE,"E316"),sQuery(id+"F0.wireOp",EDGE,"E317"),sQuery(id+"F0.wireOp",EDGE,"E318"),sQuery(id+"F0.wireOp",EDGE,"E319"),sQuery(id+"F0.wireOp",EDGE,"E320"),sQuery(id+"F0.wireOp",EDGE,"E321"),sQuery(id+"F0.wireOp",EDGE,"E322"),sQuery(id+"F0.wireOp",EDGE,"E323"),sQuery(id+"F0.wireOp",EDGE,"E324"),sQuery(id+"F0.wireOp",EDGE,"E325"),sQuery(id+"F0.wireOp",EDGE,"E326"),sQuery(id+"F0.wireOp",EDGE,"E327"),sQuery(id+"F0.wireOp",EDGE,"E328"),sQuery(id+"F0.wireOp",EDGE,"E329"),sQuery(id+"F0.wireOp",EDGE,"E330"),sQuery(id+"F0.wireOp",EDGE,"E331"),sQuery(id+"F0.wireOp",EDGE,"E332"),sQuery(id+"F0.wireOp",EDGE,"E333"),sQuery(id+"F0.wireOp",EDGE,"E334"),sQuery(id+"F0.wireOp",EDGE,"E335"),sQuery(id+"F0.wireOp",EDGE,"E336"),sQuery(id+"F0.wireOp",EDGE,"E337"),sQuery(id+"F0.wireOp",EDGE,"E338"),sQuery(id+"F0.wireOp",EDGE,"E339"),sQuery(id+"F0.wireOp",EDGE,"E340"),sQuery(id+"F0.wireOp",EDGE,"E341"),sQuery(id+"F0.wireOp",EDGE,"E342"),sQuery(id+"F0.wireOp",EDGE,"E343"),sQuery(id+"F0.wireOp",EDGE,"E344"),sQuery(id+"F0.wireOp",EDGE,"E345"),sQuery(id+"F0.wireOp",EDGE,"E346"),sQuery(id+"F0.wireOp",EDGE,"E347"),sQuery(id+"F0.wireOp",EDGE,"E348"),sQuery(id+"F0.wireOp",EDGE,"E349"),sQuery(id+"F0.wireOp",EDGE,"E350"),sQuery(id+"F0.wireOp",EDGE,"E351"),sQuery(id+"F0.wireOp",EDGE,"E352"),sQuery(id+"F0.wireOp",EDGE,"E353"),sQuery(id+"F0.wireOp",EDGE,"E354"),sQuery(id+"F0.wireOp",EDGE,"E355"),sQuery(id+"F0.wireOp",EDGE,"E356"),sQuery(id+"F0.wireOp",EDGE,"E357"),sQuery(id+"F0.wireOp",EDGE,"E358"),sQuery(id+"F0.wireOp",EDGE,"E359"),sQuery(id+"F0.wireOp",EDGE,"E360"),sQuery(id+"F0.wireOp",EDGE,"E361"),sQuery(id+"F0.wireOp",EDGE,"E362"),sQuery(id+"F0.wireOp",EDGE,"E363"),sQuery(id+"F0.wireOp",EDGE,"E364"),sQuery(id+"F0.wireOp",EDGE,"E365"),sQuery(id+"F0.wireOp",EDGE,"E366"),sQuery(id+"F0.wireOp",EDGE,"E367"),sQuery(id+"F0.wireOp",EDGE,"E368"),sQuery(id+"F0.wireOp",EDGE,"E369"),sQuery(id+"F0.wireOp",EDGE,"E370"),sQuery(id+"F0.wireOp",EDGE,"E371"),sQuery(id+"F0.wireOp",EDGE,"E372"),sQuery(id+"F0.wireOp",EDGE,"E373"),sQuery(id+"F0.wireOp",EDGE,"E374"),sQuery(id+"F0.wireOp",EDGE,"E375"),sQuery(id+"F0.wireOp",EDGE,"E376"),sQuery(id+"F0.wireOp",EDGE,"E377"),sQuery(id+"F0.wireOp",EDGE,"E378"),sQuery(id+"F0.wireOp",EDGE,"E379"),sQuery(id+"F0.wireOp",EDGE,"E380"),sQuery(id+"F0.wireOp",EDGE,"E381"),sQuery(id+"F0.wireOp",EDGE,"E382"),sQuery(id+"F0.wireOp",EDGE,"E383"),sQuery(id+"F0.wireOp",EDGE,"E384"),sQuery(id+"F0.wireOp",EDGE,"E385"),sQuery(id+"F0.wireOp",EDGE,"E386"),sQuery(id+"F0.wireOp",EDGE,"E387"),sQuery(id+"F0.wireOp",EDGE,"E388"),sQuery(id+"F0.wireOp",EDGE,"E389"),sQuery(id+"F0.wireOp",EDGE,"E390"),sQuery(id+"F0.wireOp",EDGE,"E391"),sQuery(id+"F0.wireOp",EDGE,"E392"),sQuery(id+"F0.wireOp",EDGE,"E393"),sQuery(id+"F0.wireOp",EDGE,"E394"),sQuery(id+"F0.wireOp",EDGE,"E395"),sQuery(id+"F0.wireOp",EDGE,"E396"),sQuery(id+"F0.wireOp",EDGE,"E397"),sQuery(id+"F0.wireOp",EDGE,"E398"),sQuery(id+"F0.wireOp",EDGE,"E399"),sQuery(id+"F0.wireOp",EDGE,"E400"),sQuery(id+"F0.wireOp",EDGE,"E401"),sQuery(id+"F0.wireOp",EDGE,"E402"),sQuery(id+"F0.wireOp",EDGE,"E403"),sQuery(id+"F0.wireOp",EDGE,"E404"),sQuery(id+"F0.wireOp",EDGE,"E405"),sQuery(id+"F0.wireOp",EDGE,"E406"),sQuery(id+"F0.wireOp",EDGE,"E407"),sQuery(id+"F0.wireOp",EDGE,"E408"),sQuery(id+"F0.wireOp",EDGE,"E409"),sQuery(id+"F0.wireOp",EDGE,"E410"),sQuery(id+"F0.wireOp",EDGE,"E411"),sQuery(id+"F0.wireOp",EDGE,"E412"),sQuery(id+"F0.wireOp",EDGE,"E413"),sQuery(id+"F0.wireOp",EDGE,"E414"),sQuery(id+"F0.wireOp",EDGE,"E415"),sQuery(id+"F0.wireOp",EDGE,"E416"),sQuery(id+"F0.wireOp",EDGE,"E417"),sQuery(id+"F0.wireOp",EDGE,"E418"),sQuery(id+"F0.wireOp",EDGE,"E419"),sQuery(id+"F0.wireOp",EDGE,"E420"),sQuery(id+"F0.wireOp",EDGE,"E421"),sQuery(id+"F0.wireOp",EDGE,"E422"),sQuery(id+"F0.wireOp",EDGE,"E423"),sQuery(id+"F0.wireOp",EDGE,"E424"),sQuery(id+"F0.wireOp",EDGE,"E425"),sQuery(id+"F0.wireOp",EDGE,"E426"),sQuery(id+"F0.wireOp",EDGE,"E427"),sQuery(id+"F0.wireOp",EDGE,"E428"),sQuery(id+"F0.wireOp",EDGE,"E429"),sQuery(id+"F0.wireOp",EDGE,"E430"),sQuery(id+"F0.wireOp",EDGE,"E431"),sQuery(id+"F0.wireOp",EDGE,"E432"),sQuery(id+"F0.wireOp",EDGE,"E433"),sQuery(id+"F0.wireOp",EDGE,"E434"),sQuery(id+"F0.wireOp",EDGE,"E435"),sQuery(id+"F0.wireOp",EDGE,"E436"),sQuery(id+"F0.wireOp",EDGE,"E437"),sQuery(id+"F0.wireOp",EDGE,"E438"),sQuery(id+"F0.wireOp",EDGE,"E439"),sQuery(id+"F0.wireOp",EDGE,"E440"),sQuery(id+"F0.wireOp",EDGE,"E441"),sQuery(id+"F0.wireOp",EDGE,"E442"),sQuery(id+"F0.wireOp",EDGE,"E443"),sQuery(id+"F0.wireOp",EDGE,"E444"),sQuery(id+"F0.wireOp",EDGE,"E445"),sQuery(id+"F0.wireOp",EDGE,"E446"),sQuery(id+"F0.wireOp",EDGE,"E447"),sQuery(id+"F0.wireOp",EDGE,"E448"),sQuery(id+"F0.wireOp",EDGE,"E449"),sQuery(id+"F0.wireOp",EDGE,"E450"),sQuery(id+"F0.wireOp",EDGE,"E451"),sQuery(id+"F0.wireOp",EDGE,"E452"),sQuery(id+"F0.wireOp",EDGE,"E453"),sQuery(id+"F0.wireOp",EDGE,"E454"),sQuery(id+"F0.wireOp",EDGE,"E455"),sQuery(id+"F0.wireOp",EDGE,"E456"),sQuery(id+"F0.wireOp",EDGE,"E457"),sQuery(id+"F0.wireOp",EDGE,"E458"),sQuery(id+"F0.wireOp",EDGE,"E459"),sQuery(id+"F0.wireOp",EDGE,"E460"),sQuery(id+"F0.wireOp",EDGE,"E461"),sQuery(id+"F0.wireOp",EDGE,"E462"),sQuery(id+"F0.wireOp",EDGE,"E463"),sQuery(id+"F0.wireOp",EDGE,"E464"),sQuery(id+"F0.wireOp",EDGE,"E465"),sQuery(id+"F0.wireOp",EDGE,"E466"),sQuery(id+"F0.wireOp",EDGE,"E467"),sQuery(id+"F0.wireOp",EDGE,"E468"),sQuery(id+"F0.wireOp",EDGE,"E469"),sQuery(id+"F0.wireOp",EDGE,"E470"),sQuery(id+"F0.wireOp",EDGE,"E471"),sQuery(id+"F0.wireOp",EDGE,"E472"),sQuery(id+"F0.wireOp",EDGE,"E473"),sQuery(id+"F0.wireOp",EDGE,"E474"),sQuery(id+"F0.wireOp",EDGE,"E475"),sQuery(id+"F0.wireOp",EDGE,"E476"),sQuery(id+"F0.wireOp",EDGE,"E477"),sQuery(id+"F0.wireOp",EDGE,"E478"),sQuery(id+"F0.wireOp",EDGE,"E479"),sQuery(id+"F0.wireOp",EDGE,"E480"),sQuery(id+"F0.wireOp",EDGE,"E481"),sQuery(id+"F0.wireOp",EDGE,"E482"),sQuery(id+"F0.wireOp",EDGE,"E483"),sQuery(id+"F0.wireOp",EDGE,"E484"),sQuery(id+"F0.wireOp",EDGE,"E485"),sQuery(id+"F0.wireOp",EDGE,"E486"),sQuery(id+"F0.wireOp",EDGE,"E487"),sQuery(id+"F0.wireOp",EDGE,"E488"),sQuery(id+"F0.wireOp",EDGE,"E489"),sQuery(id+"F0.wireOp",EDGE,"E490"),sQuery(id+"F0.wireOp",EDGE,"E491"),sQuery(id+"F0.wireOp",EDGE,"E492"),sQuery(id+"F0.wireOp",EDGE,"E493"),sQuery(id+"F0.wireOp",EDGE,"E494"),sQuery(id+"F0.wireOp",EDGE,"E495"),sQuery(id+"F0.wireOp",EDGE,"E496"),sQuery(id+"F0.wireOp",EDGE,"E497"),sQuery(id+"F0.wireOp",EDGE,"E498"),sQuery(id+"F0.wireOp",EDGE,"E499"),sQuery(id+"F0.wireOp",EDGE,"E500"),sQuery(id+"F0.wireOp",EDGE,"E501"),sQuery(id+"F0.wireOp",EDGE,"E502"),sQuery(id+"F0.wireOp",EDGE,"E503"),sQuery(id+"F0.wireOp",EDGE,"E504"),sQuery(id+"F0.wireOp",EDGE,"E505"),sQuery(id+"F0.wireOp",EDGE,"E506"),sQuery(id+"F0.wireOp",EDGE,"E507"),sQuery(id+"F0.wireOp",EDGE,"E508"),sQuery(id+"F0.wireOp",EDGE,"E509"),sQuery(id+"F0.wireOp",EDGE,"E510"),sQuery(id+"F0.wireOp",EDGE,"E511"),sQuery(id+"F0.wireOp",EDGE,"E512"),sQuery(id+"F0.wireOp",EDGE,"E513"),sQuery(id+"F0.wireOp",EDGE,"E514"),sQuery(id+"F0.wireOp",EDGE,"E515"),sQuery(id+"F0.wireOp",EDGE,"E516"),sQuery(id+"F0.wireOp",EDGE,"E517"),sQuery(id+"F0.wireOp",EDGE,"E518"),sQuery(id+"F0.wireOp",EDGE,"E519"),sQuery(id+"F0.wireOp",EDGE,"E520"),sQuery(id+"F0.wireOp",EDGE,"E521"),sQuery(id+"F0.wireOp",EDGE,"E522"),sQuery(id+"F0.wireOp",EDGE,"E523"),sQuery(id+"F0.wireOp",EDGE,"E524"),sQuery(id+"F0.wireOp",EDGE,"E525"),sQuery(id+"F0.wireOp",EDGE,"E526"),sQuery(id+"F0.wireOp",EDGE,"E527"),sQuery(id+"F0.wireOp",EDGE,"E528"),sQuery(id+"F0.wireOp",EDGE,"E529"),sQuery(id+"F0.wireOp",EDGE,"E530"),sQuery(id+"F0.wireOp",EDGE,"E531"),sQuery(id+"F0.wireOp",EDGE,"E532"),sQuery(id+"F0.wireOp",EDGE,"E533"),sQuery(id+"F0.wireOp",EDGE,"E534"),sQuery(id+"F0.wireOp",EDGE,"E535"),sQuery(id+"F0.wireOp",EDGE,"E536"),sQuery(id+"F0.wireOp",EDGE,"E537"),sQuery(id+"F0.wireOp",EDGE,"E538"),sQuery(id+"F0.wireOp",EDGE,"E539"),sQuery(id+"F0.wireOp",EDGE,"E540"),sQuery(id+"F0.wireOp",EDGE,"E541"),sQuery(id+"F0.wireOp",EDGE,"E542"),sQuery(id+"F0.wireOp",EDGE,"E543"),sQuery(id+"F0.wireOp",EDGE,"E544"),sQuery(id+"F0.wireOp",EDGE,"E545"),sQuery(id+"F0.wireOp",EDGE,"E546"),sQuery(id+"F0.wireOp",EDGE,"E547"),sQuery(id+"F0.wireOp",EDGE,"E548"),sQuery(id+"F0.wireOp",EDGE,"E549"),sQuery(id+"F0.wireOp",EDGE,"E550"),sQuery(id+"F0.wireOp",EDGE,"E551"),sQuery(id+"F0.wireOp",EDGE,"E552"),sQuery(id+"F0.wireOp",EDGE,"E553"),sQuery(id+"F0.wireOp",EDGE,"E554"),sQuery(id+"F0.wireOp",EDGE,"E555"),sQuery(id+"F0.wireOp",EDGE,"E556"),sQuery(id+"F0.wireOp",EDGE,"E557"),sQuery(id+"F0.wireOp",EDGE,"E558"),sQuery(id+"F0.wireOp",EDGE,"E559"),sQuery(id+"F0.wireOp",EDGE,"E560"),sQuery(id+"F0.wireOp",EDGE,"E561"),sQuery(id+"F0.wireOp",EDGE,"E562"),sQuery(id+"F0.wireOp",EDGE,"E563"),sQuery(id+"F0.wireOp",EDGE,"E564"),sQuery(id+"F0.wireOp",EDGE,"E565"),sQuery(id+"F0.wireOp",EDGE,"E566"),sQuery(id+"F0.wireOp",EDGE,"E567"),sQuery(id+"F0.wireOp",EDGE,"E568"),sQuery(id+"F0.wireOp",EDGE,"E569"),sQuery(id+"F0.wireOp",EDGE,"E570"),sQuery(id+"F0.wireOp",EDGE,"E571"),sQuery(id+"F0.wireOp",EDGE,"E572"),sQuery(id+"F0.wireOp",EDGE,"E573"),sQuery(id+"F0.wireOp",EDGE,"E574"),sQuery(id+"F0.wireOp",EDGE,"E575"),sQuery(id+"F0.wireOp",EDGE,"E576"),sQuery(id+"F0.wireOp",EDGE,"E577"),sQuery(id+"F0.wireOp",EDGE,"E578"),sQuery(id+"F0.wireOp",EDGE,"E579"),sQuery(id+"F0.wireOp",EDGE,"E580"),sQuery(id+"F0.wireOp",EDGE,"E581"),sQuery(id+"F0.wireOp",EDGE,"E582"),sQuery(id+"F0.wireOp",EDGE,"E583"),sQuery(id+"F0.wireOp",EDGE,"E584"),sQuery(id+"F0.wireOp",EDGE,"E585"),sQuery(id+"F0.wireOp",EDGE,"E586"),sQuery(id+"F0.wireOp",EDGE,"E587"),sQuery(id+"F0.wireOp",EDGE,"E588"),sQuery(id+"F0.wireOp",EDGE,"E589"),sQuery(id+"F0.wireOp",EDGE,"E590"),sQuery(id+"F0.wireOp",EDGE,"E591"),sQuery(id+"F0.wireOp",EDGE,"E592"),sQuery(id+"F0.wireOp",EDGE,"E593"),sQuery(id+"F0.wireOp",EDGE,"E594"),sQuery(id+"F0.wireOp",EDGE,"E595"),sQuery(id+"F0.wireOp",EDGE,"E596"),sQuery(id+"F0.wireOp",EDGE,"E597"),sQuery(id+"F0.wireOp",EDGE,"E598"),sQuery(id+"F0.wireOp",EDGE,"E599")])]});
            var Q1;
            Q1=qCreatedBy(makeId("Origin.pointOp"),VERTEX);
            transform(context, id + "F2", {"entities" : qUnion([Q0]), "transformType" : TransformType.SCALE_UNIFORMLY, "scale" : 0.02, "scalePoint" : qUnion([Q1]), "makeCopy" : false});
        }
        {
            var Q0;
            Q0=makeQuery(id+"F1.opExtrude","CAP_FACE",FACE,{"disambiguationData":[OSD([sQuery(id+"F0.wireOp",EDGE,"E0"),sQuery(id+"F0.wireOp",EDGE,"E1"),sQuery(id+"F0.wireOp",EDGE,"E2"),sQuery(id+"F0.wireOp",EDGE,"E3"),sQuery(id+"F0.wireOp",EDGE,"E4"),sQuery(id+"F0.wireOp",EDGE,"E5"),sQuery(id+"F0.wireOp",EDGE,"E6"),sQuery(id+"F0.wireOp",EDGE,"E7"),sQuery(id+"F0.wireOp",EDGE,"E8"),sQuery(id+"F0.wireOp",EDGE,"E9"),sQuery(id+"F0.wireOp",EDGE,"E10"),sQuery(id+"F0.wireOp",EDGE,"E11"),sQuery(id+"F0.wireOp",EDGE,"E12"),sQuery(id+"F0.wireOp",EDGE,"E13"),sQuery(id+"F0.wireOp",EDGE,"E14"),sQuery(id+"F0.wireOp",EDGE,"E15"),sQuery(id+"F0.wireOp",EDGE,"E16"),sQuery(id+"F0.wireOp",EDGE,"E17"),sQuery(id+"F0.wireOp",EDGE,"E18"),sQuery(id+"F0.wireOp",EDGE,"E19"),sQuery(id+"F0.wireOp",EDGE,"E20"),sQuery(id+"F0.wireOp",EDGE,"E21"),sQuery(id+"F0.wireOp",EDGE,"E22"),sQuery(id+"F0.wireOp",EDGE,"E23"),sQuery(id+"F0.wireOp",EDGE,"E24"),sQuery(id+"F0.wireOp",EDGE,"E25"),sQuery(id+"F0.wireOp",EDGE,"E26"),sQuery(id+"F0.wireOp",EDGE,"E27"),sQuery(id+"F0.wireOp",EDGE,"E28"),sQuery(id+"F0.wireOp",EDGE,"E29"),sQuery(id+"F0.wireOp",EDGE,"E30"),sQuery(id+"F0.wireOp",EDGE,"E31"),sQuery(id+"F0.wireOp",EDGE,"E32"),sQuery(id+"F0.wireOp",EDGE,"E33"),sQuery(id+"F0.wireOp",EDGE,"E34"),sQuery(id+"F0.wireOp",EDGE,"E35"),sQuery(id+"F0.wireOp",EDGE,"E36"),sQuery(id+"F0.wireOp",EDGE,"E37"),sQuery(id+"F0.wireOp",EDGE,"E38"),sQuery(id+"F0.wireOp",EDGE,"E39"),sQuery(id+"F0.wireOp",EDGE,"E40"),sQuery(id+"F0.wireOp",EDGE,"E41"),sQuery(id+"F0.wireOp",EDGE,"E42"),sQuery(id+"F0.wireOp",EDGE,"E43"),sQuery(id+"F0.wireOp",EDGE,"E44"),sQuery(id+"F0.wireOp",EDGE,"E45"),sQuery(id+"F0.wireOp",EDGE,"E46"),sQuery(id+"F0.wireOp",EDGE,"E47"),sQuery(id+"F0.wireOp",EDGE,"E48"),sQuery(id+"F0.wireOp",EDGE,"E49"),sQuery(id+"F0.wireOp",EDGE,"E50"),sQuery(id+"F0.wireOp",EDGE,"E51"),sQuery(id+"F0.wireOp",EDGE,"E52"),sQuery(id+"F0.wireOp",EDGE,"E53"),sQuery(id+"F0.wireOp",EDGE,"E54"),sQuery(id+"F0.wireOp",EDGE,"E55"),sQuery(id+"F0.wireOp",EDGE,"E56"),sQuery(id+"F0.wireOp",EDGE,"E57"),sQuery(id+"F0.wireOp",EDGE,"E58"),sQuery(id+"F0.wireOp",EDGE,"E59"),sQuery(id+"F0.wireOp",EDGE,"E60"),sQuery(id+"F0.wireOp",EDGE,"E61"),sQuery(id+"F0.wireOp",EDGE,"E62"),sQuery(id+"F0.wireOp",EDGE,"E63"),sQuery(id+"F0.wireOp",EDGE,"E64"),sQuery(id+"F0.wireOp",EDGE,"E65"),sQuery(id+"F0.wireOp",EDGE,"E66"),sQuery(id+"F0.wireOp",EDGE,"E67"),sQuery(id+"F0.wireOp",EDGE,"E68"),sQuery(id+"F0.wireOp",EDGE,"E69"),sQuery(id+"F0.wireOp",EDGE,"E70"),sQuery(id+"F0.wireOp",EDGE,"E71"),sQuery(id+"F0.wireOp",EDGE,"E72"),sQuery(id+"F0.wireOp",EDGE,"E73"),sQuery(id+"F0.wireOp",EDGE,"E74"),sQuery(id+"F0.wireOp",EDGE,"E75"),sQuery(id+"F0.wireOp",EDGE,"E76"),sQuery(id+"F0.wireOp",EDGE,"E77"),sQuery(id+"F0.wireOp",EDGE,"E78"),sQuery(id+"F0.wireOp",EDGE,"E79"),sQuery(id+"F0.wireOp",EDGE,"E80"),sQuery(id+"F0.wireOp",EDGE,"E81"),sQuery(id+"F0.wireOp",EDGE,"E82"),sQuery(id+"F0.wireOp",EDGE,"E83"),sQuery(id+"F0.wireOp",EDGE,"E84"),sQuery(id+"F0.wireOp",EDGE,"E85"),sQuery(id+"F0.wireOp",EDGE,"E86"),sQuery(id+"F0.wireOp",EDGE,"E87"),sQuery(id+"F0.wireOp",EDGE,"E88"),sQuery(id+"F0.wireOp",EDGE,"E89"),sQuery(id+"F0.wireOp",EDGE,"E90"),sQuery(id+"F0.wireOp",EDGE,"E91"),sQuery(id+"F0.wireOp",EDGE,"E92"),sQuery(id+"F0.wireOp",EDGE,"E93"),sQuery(id+"F0.wireOp",EDGE,"E94"),sQuery(id+"F0.wireOp",EDGE,"E95"),sQuery(id+"F0.wireOp",EDGE,"E96"),sQuery(id+"F0.wireOp",EDGE,"E97"),sQuery(id+"F0.wireOp",EDGE,"E98"),sQuery(id+"F0.wireOp",EDGE,"E99"),sQuery(id+"F0.wireOp",EDGE,"E100"),sQuery(id+"F0.wireOp",EDGE,"E101"),sQuery(id+"F0.wireOp",EDGE,"E102"),sQuery(id+"F0.wireOp",EDGE,"E103"),sQuery(id+"F0.wireOp",EDGE,"E104"),sQuery(id+"F0.wireOp",EDGE,"E105"),sQuery(id+"F0.wireOp",EDGE,"E106"),sQuery(id+"F0.wireOp",EDGE,"E107"),sQuery(id+"F0.wireOp",EDGE,"E108"),sQuery(id+"F0.wireOp",EDGE,"E109"),sQuery(id+"F0.wireOp",EDGE,"E110"),sQuery(id+"F0.wireOp",EDGE,"E111"),sQuery(id+"F0.wireOp",EDGE,"E112"),sQuery(id+"F0.wireOp",EDGE,"E113"),sQuery(id+"F0.wireOp",EDGE,"E114"),sQuery(id+"F0.wireOp",EDGE,"E115"),sQuery(id+"F0.wireOp",EDGE,"E116"),sQuery(id+"F0.wireOp",EDGE,"E117"),sQuery(id+"F0.wireOp",EDGE,"E118"),sQuery(id+"F0.wireOp",EDGE,"E119"),sQuery(id+"F0.wireOp",EDGE,"E120"),sQuery(id+"F0.wireOp",EDGE,"E121"),sQuery(id+"F0.wireOp",EDGE,"E122"),sQuery(id+"F0.wireOp",EDGE,"E123"),sQuery(id+"F0.wireOp",EDGE,"E124"),sQuery(id+"F0.wireOp",EDGE,"E125"),sQuery(id+"F0.wireOp",EDGE,"E126"),sQuery(id+"F0.wireOp",EDGE,"E127"),sQuery(id+"F0.wireOp",EDGE,"E128"),sQuery(id+"F0.wireOp",EDGE,"E129"),sQuery(id+"F0.wireOp",EDGE,"E130"),sQuery(id+"F0.wireOp",EDGE,"E131"),sQuery(id+"F0.wireOp",EDGE,"E132"),sQuery(id+"F0.wireOp",EDGE,"E133"),sQuery(id+"F0.wireOp",EDGE,"E134"),sQuery(id+"F0.wireOp",EDGE,"E135"),sQuery(id+"F0.wireOp",EDGE,"E136"),sQuery(id+"F0.wireOp",EDGE,"E137"),sQuery(id+"F0.wireOp",EDGE,"E138"),sQuery(id+"F0.wireOp",EDGE,"E139"),sQuery(id+"F0.wireOp",EDGE,"E140"),sQuery(id+"F0.wireOp",EDGE,"E141"),sQuery(id+"F0.wireOp",EDGE,"E142"),sQuery(id+"F0.wireOp",EDGE,"E143"),sQuery(id+"F0.wireOp",EDGE,"E144"),sQuery(id+"F0.wireOp",EDGE,"E145"),sQuery(id+"F0.wireOp",EDGE,"E146"),sQuery(id+"F0.wireOp",EDGE,"E147"),sQuery(id+"F0.wireOp",EDGE,"E148"),sQuery(id+"F0.wireOp",EDGE,"E149"),sQuery(id+"F0.wireOp",EDGE,"E150"),sQuery(id+"F0.wireOp",EDGE,"E151"),sQuery(id+"F0.wireOp",EDGE,"E152"),sQuery(id+"F0.wireOp",EDGE,"E153"),sQuery(id+"F0.wireOp",EDGE,"E154"),sQuery(id+"F0.wireOp",EDGE,"E155"),sQuery(id+"F0.wireOp",EDGE,"E156"),sQuery(id+"F0.wireOp",EDGE,"E157"),sQuery(id+"F0.wireOp",EDGE,"E158"),sQuery(id+"F0.wireOp",EDGE,"E159"),sQuery(id+"F0.wireOp",EDGE,"E160"),sQuery(id+"F0.wireOp",EDGE,"E161"),sQuery(id+"F0.wireOp",EDGE,"E162"),sQuery(id+"F0.wireOp",EDGE,"E163"),sQuery(id+"F0.wireOp",EDGE,"E164"),sQuery(id+"F0.wireOp",EDGE,"E165"),sQuery(id+"F0.wireOp",EDGE,"E166"),sQuery(id+"F0.wireOp",EDGE,"E167"),sQuery(id+"F0.wireOp",EDGE,"E168"),sQuery(id+"F0.wireOp",EDGE,"E169"),sQuery(id+"F0.wireOp",EDGE,"E170"),sQuery(id+"F0.wireOp",EDGE,"E171"),sQuery(id+"F0.wireOp",EDGE,"E172"),sQuery(id+"F0.wireOp",EDGE,"E173"),sQuery(id+"F0.wireOp",EDGE,"E174"),sQuery(id+"F0.wireOp",EDGE,"E175"),sQuery(id+"F0.wireOp",EDGE,"E176"),sQuery(id+"F0.wireOp",EDGE,"E177"),sQuery(id+"F0.wireOp",EDGE,"E178"),sQuery(id+"F0.wireOp",EDGE,"E179"),sQuery(id+"F0.wireOp",EDGE,"E180"),sQuery(id+"F0.wireOp",EDGE,"E181"),sQuery(id+"F0.wireOp",EDGE,"E182"),sQuery(id+"F0.wireOp",EDGE,"E183"),sQuery(id+"F0.wireOp",EDGE,"E184"),sQuery(id+"F0.wireOp",EDGE,"E185"),sQuery(id+"F0.wireOp",EDGE,"E186"),sQuery(id+"F0.wireOp",EDGE,"E187"),sQuery(id+"F0.wireOp",EDGE,"E188"),sQuery(id+"F0.wireOp",EDGE,"E189"),sQuery(id+"F0.wireOp",EDGE,"E190"),sQuery(id+"F0.wireOp",EDGE,"E191"),sQuery(id+"F0.wireOp",EDGE,"E192"),sQuery(id+"F0.wireOp",EDGE,"E193"),sQuery(id+"F0.wireOp",EDGE,"E194"),sQuery(id+"F0.wireOp",EDGE,"E195"),sQuery(id+"F0.wireOp",EDGE,"E196"),sQuery(id+"F0.wireOp",EDGE,"E197"),sQuery(id+"F0.wireOp",EDGE,"E198"),sQuery(id+"F0.wireOp",EDGE,"E199"),sQuery(id+"F0.wireOp",EDGE,"E200"),sQuery(id+"F0.wireOp",EDGE,"E201"),sQuery(id+"F0.wireOp",EDGE,"E202"),sQuery(id+"F0.wireOp",EDGE,"E203"),sQuery(id+"F0.wireOp",EDGE,"E204"),sQuery(id+"F0.wireOp",EDGE,"E205"),sQuery(id+"F0.wireOp",EDGE,"E206"),sQuery(id+"F0.wireOp",EDGE,"E207"),sQuery(id+"F0.wireOp",EDGE,"E208"),sQuery(id+"F0.wireOp",EDGE,"E209"),sQuery(id+"F0.wireOp",EDGE,"E210"),sQuery(id+"F0.wireOp",EDGE,"E211"),sQuery(id+"F0.wireOp",EDGE,"E212"),sQuery(id+"F0.wireOp",EDGE,"E213"),sQuery(id+"F0.wireOp",EDGE,"E214"),sQuery(id+"F0.wireOp",EDGE,"E215"),sQuery(id+"F0.wireOp",EDGE,"E216"),sQuery(id+"F0.wireOp",EDGE,"E217"),sQuery(id+"F0.wireOp",EDGE,"E218"),sQuery(id+"F0.wireOp",EDGE,"E219"),sQuery(id+"F0.wireOp",EDGE,"E220"),sQuery(id+"F0.wireOp",EDGE,"E221"),sQuery(id+"F0.wireOp",EDGE,"E222"),sQuery(id+"F0.wireOp",EDGE,"E223"),sQuery(id+"F0.wireOp",EDGE,"E224"),sQuery(id+"F0.wireOp",EDGE,"E225"),sQuery(id+"F0.wireOp",EDGE,"E226"),sQuery(id+"F0.wireOp",EDGE,"E227"),sQuery(id+"F0.wireOp",EDGE,"E228"),sQuery(id+"F0.wireOp",EDGE,"E229"),sQuery(id+"F0.wireOp",EDGE,"E230"),sQuery(id+"F0.wireOp",EDGE,"E231"),sQuery(id+"F0.wireOp",EDGE,"E232"),sQuery(id+"F0.wireOp",EDGE,"E233"),sQuery(id+"F0.wireOp",EDGE,"E234"),sQuery(id+"F0.wireOp",EDGE,"E235"),sQuery(id+"F0.wireOp",EDGE,"E236"),sQuery(id+"F0.wireOp",EDGE,"E237"),sQuery(id+"F0.wireOp",EDGE,"E238"),sQuery(id+"F0.wireOp",EDGE,"E239"),sQuery(id+"F0.wireOp",EDGE,"E240"),sQuery(id+"F0.wireOp",EDGE,"E241"),sQuery(id+"F0.wireOp",EDGE,"E242"),sQuery(id+"F0.wireOp",EDGE,"E243"),sQuery(id+"F0.wireOp",EDGE,"E244"),sQuery(id+"F0.wireOp",EDGE,"E245"),sQuery(id+"F0.wireOp",EDGE,"E246"),sQuery(id+"F0.wireOp",EDGE,"E247"),sQuery(id+"F0.wireOp",EDGE,"E248"),sQuery(id+"F0.wireOp",EDGE,"E249"),sQuery(id+"F0.wireOp",EDGE,"E250"),sQuery(id+"F0.wireOp",EDGE,"E251"),sQuery(id+"F0.wireOp",EDGE,"E252"),sQuery(id+"F0.wireOp",EDGE,"E253"),sQuery(id+"F0.wireOp",EDGE,"E254"),sQuery(id+"F0.wireOp",EDGE,"E255"),sQuery(id+"F0.wireOp",EDGE,"E256"),sQuery(id+"F0.wireOp",EDGE,"E257"),sQuery(id+"F0.wireOp",EDGE,"E258"),sQuery(id+"F0.wireOp",EDGE,"E259"),sQuery(id+"F0.wireOp",EDGE,"E260"),sQuery(id+"F0.wireOp",EDGE,"E261"),sQuery(id+"F0.wireOp",EDGE,"E262"),sQuery(id+"F0.wireOp",EDGE,"E263"),sQuery(id+"F0.wireOp",EDGE,"E264"),sQuery(id+"F0.wireOp",EDGE,"E265"),sQuery(id+"F0.wireOp",EDGE,"E266"),sQuery(id+"F0.wireOp",EDGE,"E267"),sQuery(id+"F0.wireOp",EDGE,"E268"),sQuery(id+"F0.wireOp",EDGE,"E269"),sQuery(id+"F0.wireOp",EDGE,"E270"),sQuery(id+"F0.wireOp",EDGE,"E271"),sQuery(id+"F0.wireOp",EDGE,"E272"),sQuery(id+"F0.wireOp",EDGE,"E273"),sQuery(id+"F0.wireOp",EDGE,"E274"),sQuery(id+"F0.wireOp",EDGE,"E275"),sQuery(id+"F0.wireOp",EDGE,"E276"),sQuery(id+"F0.wireOp",EDGE,"E277"),sQuery(id+"F0.wireOp",EDGE,"E278"),sQuery(id+"F0.wireOp",EDGE,"E279"),sQuery(id+"F0.wireOp",EDGE,"E280"),sQuery(id+"F0.wireOp",EDGE,"E281"),sQuery(id+"F0.wireOp",EDGE,"E282"),sQuery(id+"F0.wireOp",EDGE,"E283"),sQuery(id+"F0.wireOp",EDGE,"E284"),sQuery(id+"F0.wireOp",EDGE,"E285"),sQuery(id+"F0.wireOp",EDGE,"E286"),sQuery(id+"F0.wireOp",EDGE,"E287"),sQuery(id+"F0.wireOp",EDGE,"E288"),sQuery(id+"F0.wireOp",EDGE,"E289"),sQuery(id+"F0.wireOp",EDGE,"E290"),sQuery(id+"F0.wireOp",EDGE,"E291"),sQuery(id+"F0.wireOp",EDGE,"E292"),sQuery(id+"F0.wireOp",EDGE,"E293"),sQuery(id+"F0.wireOp",EDGE,"E294"),sQuery(id+"F0.wireOp",EDGE,"E295"),sQuery(id+"F0.wireOp",EDGE,"E296"),sQuery(id+"F0.wireOp",EDGE,"E297"),sQuery(id+"F0.wireOp",EDGE,"E298"),sQuery(id+"F0.wireOp",EDGE,"E299"),sQuery(id+"F0.wireOp",EDGE,"E300"),sQuery(id+"F0.wireOp",EDGE,"E301"),sQuery(id+"F0.wireOp",EDGE,"E302"),sQuery(id+"F0.wireOp",EDGE,"E303"),sQuery(id+"F0.wireOp",EDGE,"E304"),sQuery(id+"F0.wireOp",EDGE,"E305"),sQuery(id+"F0.wireOp",EDGE,"E306"),sQuery(id+"F0.wireOp",EDGE,"E307"),sQuery(id+"F0.wireOp",EDGE,"E308"),sQuery(id+"F0.wireOp",EDGE,"E309"),sQuery(id+"F0.wireOp",EDGE,"E310"),sQuery(id+"F0.wireOp",EDGE,"E311"),sQuery(id+"F0.wireOp",EDGE,"E312"),sQuery(id+"F0.wireOp",EDGE,"E313"),sQuery(id+"F0.wireOp",EDGE,"E314"),sQuery(id+"F0.wireOp",EDGE,"E315"),sQuery(id+"F0.wireOp",EDGE,"E316"),sQuery(id+"F0.wireOp",EDGE,"E317"),sQuery(id+"F0.wireOp",EDGE,"E318"),sQuery(id+"F0.wireOp",EDGE,"E319"),sQuery(id+"F0.wireOp",EDGE,"E320"),sQuery(id+"F0.wireOp",EDGE,"E321"),sQuery(id+"F0.wireOp",EDGE,"E322"),sQuery(id+"F0.wireOp",EDGE,"E323"),sQuery(id+"F0.wireOp",EDGE,"E324"),sQuery(id+"F0.wireOp",EDGE,"E325"),sQuery(id+"F0.wireOp",EDGE,"E326"),sQuery(id+"F0.wireOp",EDGE,"E327"),sQuery(id+"F0.wireOp",EDGE,"E328"),sQuery(id+"F0.wireOp",EDGE,"E329"),sQuery(id+"F0.wireOp",EDGE,"E330"),sQuery(id+"F0.wireOp",EDGE,"E331"),sQuery(id+"F0.wireOp",EDGE,"E332"),sQuery(id+"F0.wireOp",EDGE,"E333"),sQuery(id+"F0.wireOp",EDGE,"E334"),sQuery(id+"F0.wireOp",EDGE,"E335"),sQuery(id+"F0.wireOp",EDGE,"E336"),sQuery(id+"F0.wireOp",EDGE,"E337"),sQuery(id+"F0.wireOp",EDGE,"E338"),sQuery(id+"F0.wireOp",EDGE,"E339"),sQuery(id+"F0.wireOp",EDGE,"E340"),sQuery(id+"F0.wireOp",EDGE,"E341"),sQuery(id+"F0.wireOp",EDGE,"E342"),sQuery(id+"F0.wireOp",EDGE,"E343"),sQuery(id+"F0.wireOp",EDGE,"E344"),sQuery(id+"F0.wireOp",EDGE,"E345"),sQuery(id+"F0.wireOp",EDGE,"E346"),sQuery(id+"F0.wireOp",EDGE,"E347"),sQuery(id+"F0.wireOp",EDGE,"E348"),sQuery(id+"F0.wireOp",EDGE,"E349"),sQuery(id+"F0.wireOp",EDGE,"E350"),sQuery(id+"F0.wireOp",EDGE,"E351"),sQuery(id+"F0.wireOp",EDGE,"E352"),sQuery(id+"F0.wireOp",EDGE,"E353"),sQuery(id+"F0.wireOp",EDGE,"E354"),sQuery(id+"F0.wireOp",EDGE,"E355"),sQuery(id+"F0.wireOp",EDGE,"E356"),sQuery(id+"F0.wireOp",EDGE,"E357"),sQuery(id+"F0.wireOp",EDGE,"E358"),sQuery(id+"F0.wireOp",EDGE,"E359"),sQuery(id+"F0.wireOp",EDGE,"E360"),sQuery(id+"F0.wireOp",EDGE,"E361"),sQuery(id+"F0.wireOp",EDGE,"E362"),sQuery(id+"F0.wireOp",EDGE,"E363"),sQuery(id+"F0.wireOp",EDGE,"E364"),sQuery(id+"F0.wireOp",EDGE,"E365"),sQuery(id+"F0.wireOp",EDGE,"E366"),sQuery(id+"F0.wireOp",EDGE,"E367"),sQuery(id+"F0.wireOp",EDGE,"E368"),sQuery(id+"F0.wireOp",EDGE,"E369"),sQuery(id+"F0.wireOp",EDGE,"E370"),sQuery(id+"F0.wireOp",EDGE,"E371"),sQuery(id+"F0.wireOp",EDGE,"E372"),sQuery(id+"F0.wireOp",EDGE,"E373"),sQuery(id+"F0.wireOp",EDGE,"E374"),sQuery(id+"F0.wireOp",EDGE,"E375"),sQuery(id+"F0.wireOp",EDGE,"E376"),sQuery(id+"F0.wireOp",EDGE,"E377"),sQuery(id+"F0.wireOp",EDGE,"E378"),sQuery(id+"F0.wireOp",EDGE,"E379"),sQuery(id+"F0.wireOp",EDGE,"E380"),sQuery(id+"F0.wireOp",EDGE,"E381"),sQuery(id+"F0.wireOp",EDGE,"E382"),sQuery(id+"F0.wireOp",EDGE,"E383"),sQuery(id+"F0.wireOp",EDGE,"E384"),sQuery(id+"F0.wireOp",EDGE,"E385"),sQuery(id+"F0.wireOp",EDGE,"E386"),sQuery(id+"F0.wireOp",EDGE,"E387"),sQuery(id+"F0.wireOp",EDGE,"E388"),sQuery(id+"F0.wireOp",EDGE,"E389"),sQuery(id+"F0.wireOp",EDGE,"E390"),sQuery(id+"F0.wireOp",EDGE,"E391"),sQuery(id+"F0.wireOp",EDGE,"E392"),sQuery(id+"F0.wireOp",EDGE,"E393"),sQuery(id+"F0.wireOp",EDGE,"E394"),sQuery(id+"F0.wireOp",EDGE,"E395"),sQuery(id+"F0.wireOp",EDGE,"E396"),sQuery(id+"F0.wireOp",EDGE,"E397"),sQuery(id+"F0.wireOp",EDGE,"E398"),sQuery(id+"F0.wireOp",EDGE,"E399"),sQuery(id+"F0.wireOp",EDGE,"E400"),sQuery(id+"F0.wireOp",EDGE,"E401"),sQuery(id+"F0.wireOp",EDGE,"E402"),sQuery(id+"F0.wireOp",EDGE,"E403"),sQuery(id+"F0.wireOp",EDGE,"E404"),sQuery(id+"F0.wireOp",EDGE,"E405"),sQuery(id+"F0.wireOp",EDGE,"E406"),sQuery(id+"F0.wireOp",EDGE,"E407"),sQuery(id+"F0.wireOp",EDGE,"E408"),sQuery(id+"F0.wireOp",EDGE,"E409"),sQuery(id+"F0.wireOp",EDGE,"E410"),sQuery(id+"F0.wireOp",EDGE,"E411"),sQuery(id+"F0.wireOp",EDGE,"E412"),sQuery(id+"F0.wireOp",EDGE,"E413"),sQuery(id+"F0.wireOp",EDGE,"E414"),sQuery(id+"F0.wireOp",EDGE,"E415"),sQuery(id+"F0.wireOp",EDGE,"E416"),sQuery(id+"F0.wireOp",EDGE,"E417"),sQuery(id+"F0.wireOp",EDGE,"E418"),sQuery(id+"F0.wireOp",EDGE,"E419"),sQuery(id+"F0.wireOp",EDGE,"E420"),sQuery(id+"F0.wireOp",EDGE,"E421"),sQuery(id+"F0.wireOp",EDGE,"E422"),sQuery(id+"F0.wireOp",EDGE,"E423"),sQuery(id+"F0.wireOp",EDGE,"E424"),sQuery(id+"F0.wireOp",EDGE,"E425"),sQuery(id+"F0.wireOp",EDGE,"E426"),sQuery(id+"F0.wireOp",EDGE,"E427"),sQuery(id+"F0.wireOp",EDGE,"E428"),sQuery(id+"F0.wireOp",EDGE,"E429"),sQuery(id+"F0.wireOp",EDGE,"E430"),sQuery(id+"F0.wireOp",EDGE,"E431"),sQuery(id+"F0.wireOp",EDGE,"E432"),sQuery(id+"F0.wireOp",EDGE,"E433"),sQuery(id+"F0.wireOp",EDGE,"E434"),sQuery(id+"F0.wireOp",EDGE,"E435"),sQuery(id+"F0.wireOp",EDGE,"E436"),sQuery(id+"F0.wireOp",EDGE,"E437"),sQuery(id+"F0.wireOp",EDGE,"E438"),sQuery(id+"F0.wireOp",EDGE,"E439"),sQuery(id+"F0.wireOp",EDGE,"E440"),sQuery(id+"F0.wireOp",EDGE,"E441"),sQuery(id+"F0.wireOp",EDGE,"E442"),sQuery(id+"F0.wireOp",EDGE,"E443"),sQuery(id+"F0.wireOp",EDGE,"E444"),sQuery(id+"F0.wireOp",EDGE,"E445"),sQuery(id+"F0.wireOp",EDGE,"E446"),sQuery(id+"F0.wireOp",EDGE,"E447"),sQuery(id+"F0.wireOp",EDGE,"E448"),sQuery(id+"F0.wireOp",EDGE,"E449"),sQuery(id+"F0.wireOp",EDGE,"E450"),sQuery(id+"F0.wireOp",EDGE,"E451"),sQuery(id+"F0.wireOp",EDGE,"E452"),sQuery(id+"F0.wireOp",EDGE,"E453"),sQuery(id+"F0.wireOp",EDGE,"E454"),sQuery(id+"F0.wireOp",EDGE,"E455"),sQuery(id+"F0.wireOp",EDGE,"E456"),sQuery(id+"F0.wireOp",EDGE,"E457"),sQuery(id+"F0.wireOp",EDGE,"E458"),sQuery(id+"F0.wireOp",EDGE,"E459"),sQuery(id+"F0.wireOp",EDGE,"E460"),sQuery(id+"F0.wireOp",EDGE,"E461"),sQuery(id+"F0.wireOp",EDGE,"E462"),sQuery(id+"F0.wireOp",EDGE,"E463"),sQuery(id+"F0.wireOp",EDGE,"E464"),sQuery(id+"F0.wireOp",EDGE,"E465"),sQuery(id+"F0.wireOp",EDGE,"E466"),sQuery(id+"F0.wireOp",EDGE,"E467"),sQuery(id+"F0.wireOp",EDGE,"E468"),sQuery(id+"F0.wireOp",EDGE,"E469"),sQuery(id+"F0.wireOp",EDGE,"E470"),sQuery(id+"F0.wireOp",EDGE,"E471"),sQuery(id+"F0.wireOp",EDGE,"E472"),sQuery(id+"F0.wireOp",EDGE,"E473"),sQuery(id+"F0.wireOp",EDGE,"E474"),sQuery(id+"F0.wireOp",EDGE,"E475"),sQuery(id+"F0.wireOp",EDGE,"E476"),sQuery(id+"F0.wireOp",EDGE,"E477"),sQuery(id+"F0.wireOp",EDGE,"E478"),sQuery(id+"F0.wireOp",EDGE,"E479"),sQuery(id+"F0.wireOp",EDGE,"E480"),sQuery(id+"F0.wireOp",EDGE,"E481"),sQuery(id+"F0.wireOp",EDGE,"E482"),sQuery(id+"F0.wireOp",EDGE,"E483"),sQuery(id+"F0.wireOp",EDGE,"E484"),sQuery(id+"F0.wireOp",EDGE,"E485"),sQuery(id+"F0.wireOp",EDGE,"E486"),sQuery(id+"F0.wireOp",EDGE,"E487"),sQuery(id+"F0.wireOp",EDGE,"E488"),sQuery(id+"F0.wireOp",EDGE,"E489"),sQuery(id+"F0.wireOp",EDGE,"E490"),sQuery(id+"F0.wireOp",EDGE,"E491"),sQuery(id+"F0.wireOp",EDGE,"E492"),sQuery(id+"F0.wireOp",EDGE,"E493"),sQuery(id+"F0.wireOp",EDGE,"E494"),sQuery(id+"F0.wireOp",EDGE,"E495"),sQuery(id+"F0.wireOp",EDGE,"E496"),sQuery(id+"F0.wireOp",EDGE,"E497"),sQuery(id+"F0.wireOp",EDGE,"E498"),sQuery(id+"F0.wireOp",EDGE,"E499"),sQuery(id+"F0.wireOp",EDGE,"E500"),sQuery(id+"F0.wireOp",EDGE,"E501"),sQuery(id+"F0.wireOp",EDGE,"E502"),sQuery(id+"F0.wireOp",EDGE,"E503"),sQuery(id+"F0.wireOp",EDGE,"E504"),sQuery(id+"F0.wireOp",EDGE,"E505"),sQuery(id+"F0.wireOp",EDGE,"E506"),sQuery(id+"F0.wireOp",EDGE,"E507"),sQuery(id+"F0.wireOp",EDGE,"E508"),sQuery(id+"F0.wireOp",EDGE,"E509"),sQuery(id+"F0.wireOp",EDGE,"E510"),sQuery(id+"F0.wireOp",EDGE,"E511"),sQuery(id+"F0.wireOp",EDGE,"E512"),sQuery(id+"F0.wireOp",EDGE,"E513"),sQuery(id+"F0.wireOp",EDGE,"E514"),sQuery(id+"F0.wireOp",EDGE,"E515"),sQuery(id+"F0.wireOp",EDGE,"E516"),sQuery(id+"F0.wireOp",EDGE,"E517"),sQuery(id+"F0.wireOp",EDGE,"E518"),sQuery(id+"F0.wireOp",EDGE,"E519"),sQuery(id+"F0.wireOp",EDGE,"E520"),sQuery(id+"F0.wireOp",EDGE,"E521"),sQuery(id+"F0.wireOp",EDGE,"E522"),sQuery(id+"F0.wireOp",EDGE,"E523"),sQuery(id+"F0.wireOp",EDGE,"E524"),sQuery(id+"F0.wireOp",EDGE,"E525"),sQuery(id+"F0.wireOp",EDGE,"E526"),sQuery(id+"F0.wireOp",EDGE,"E527"),sQuery(id+"F0.wireOp",EDGE,"E528"),sQuery(id+"F0.wireOp",EDGE,"E529"),sQuery(id+"F0.wireOp",EDGE,"E530"),sQuery(id+"F0.wireOp",EDGE,"E531"),sQuery(id+"F0.wireOp",EDGE,"E532"),sQuery(id+"F0.wireOp",EDGE,"E533"),sQuery(id+"F0.wireOp",EDGE,"E534"),sQuery(id+"F0.wireOp",EDGE,"E535"),sQuery(id+"F0.wireOp",EDGE,"E536"),sQuery(id+"F0.wireOp",EDGE,"E537"),sQuery(id+"F0.wireOp",EDGE,"E538"),sQuery(id+"F0.wireOp",EDGE,"E539"),sQuery(id+"F0.wireOp",EDGE,"E540"),sQuery(id+"F0.wireOp",EDGE,"E541"),sQuery(id+"F0.wireOp",EDGE,"E542"),sQuery(id+"F0.wireOp",EDGE,"E543"),sQuery(id+"F0.wireOp",EDGE,"E544"),sQuery(id+"F0.wireOp",EDGE,"E545"),sQuery(id+"F0.wireOp",EDGE,"E546"),sQuery(id+"F0.wireOp",EDGE,"E547"),sQuery(id+"F0.wireOp",EDGE,"E548"),sQuery(id+"F0.wireOp",EDGE,"E549"),sQuery(id+"F0.wireOp",EDGE,"E550"),sQuery(id+"F0.wireOp",EDGE,"E551"),sQuery(id+"F0.wireOp",EDGE,"E552"),sQuery(id+"F0.wireOp",EDGE,"E553"),sQuery(id+"F0.wireOp",EDGE,"E554"),sQuery(id+"F0.wireOp",EDGE,"E555"),sQuery(id+"F0.wireOp",EDGE,"E556"),sQuery(id+"F0.wireOp",EDGE,"E557"),sQuery(id+"F0.wireOp",EDGE,"E558"),sQuery(id+"F0.wireOp",EDGE,"E559"),sQuery(id+"F0.wireOp",EDGE,"E560"),sQuery(id+"F0.wireOp",EDGE,"E561"),sQuery(id+"F0.wireOp",EDGE,"E562"),sQuery(id+"F0.wireOp",EDGE,"E563"),sQuery(id+"F0.wireOp",EDGE,"E564"),sQuery(id+"F0.wireOp",EDGE,"E565"),sQuery(id+"F0.wireOp",EDGE,"E566"),sQuery(id+"F0.wireOp",EDGE,"E567"),sQuery(id+"F0.wireOp",EDGE,"E568"),sQuery(id+"F0.wireOp",EDGE,"E569"),sQuery(id+"F0.wireOp",EDGE,"E570"),sQuery(id+"F0.wireOp",EDGE,"E571"),sQuery(id+"F0.wireOp",EDGE,"E572"),sQuery(id+"F0.wireOp",EDGE,"E573"),sQuery(id+"F0.wireOp",EDGE,"E574"),sQuery(id+"F0.wireOp",EDGE,"E575"),sQuery(id+"F0.wireOp",EDGE,"E576"),sQuery(id+"F0.wireOp",EDGE,"E577"),sQuery(id+"F0.wireOp",EDGE,"E578"),sQuery(id+"F0.wireOp",EDGE,"E579"),sQuery(id+"F0.wireOp",EDGE,"E580"),sQuery(id+"F0.wireOp",EDGE,"E581"),sQuery(id+"F0.wireOp",EDGE,"E582"),sQuery(id+"F0.wireOp",EDGE,"E583"),sQuery(id+"F0.wireOp",EDGE,"E584"),sQuery(id+"F0.wireOp",EDGE,"E585"),sQuery(id+"F0.wireOp",EDGE,"E586"),sQuery(id+"F0.wireOp",EDGE,"E587"),sQuery(id+"F0.wireOp",EDGE,"E588"),sQuery(id+"F0.wireOp",EDGE,"E589"),sQuery(id+"F0.wireOp",EDGE,"E590"),sQuery(id+"F0.wireOp",EDGE,"E591"),sQuery(id+"F0.wireOp",EDGE,"E592"),sQuery(id+"F0.wireOp",EDGE,"E593"),sQuery(id+"F0.wireOp",EDGE,"E594"),sQuery(id+"F0.wireOp",EDGE,"E595"),sQuery(id+"F0.wireOp",EDGE,"E596"),sQuery(id+"F0.wireOp",EDGE,"E597"),sQuery(id+"F0.wireOp",EDGE,"E598"),sQuery(id+"F0.wireOp",EDGE,"E599")])],"isStart":false});
            var sketch = newSketch(context, id + "F3", { "sketchPlane" : qUnion([Q0])});
            skPoint(sketch, "E600", {"position": v(-4.59, 0) * mm});
            skCircle(sketch, "E601", {"center": v(-4.59, 0) * mm, "radius": 2.5 * mm});
            skSolve(sketch);
        }
        {
            var Q0;
            Q0=makeQuery(id+"F3.imprint","IMPRINT",FACE,{"disambiguationData":[TD([[makeQuery(id+"F3.imprint","IMPRINT",EDGE,{"derivedFrom":sQuery(id+"F3.wireOp",EDGE,"E601")}),1.0]])]});
            extrude(context, id + "F4", {"entities" : qUnion([Q0]), "operationType" : NewBodyOperationType.REMOVE, "oppositeDirection" : true, "depth" : 25.4 * mm, "offsetDistance" : 25.4 * mm});
        }
    });
